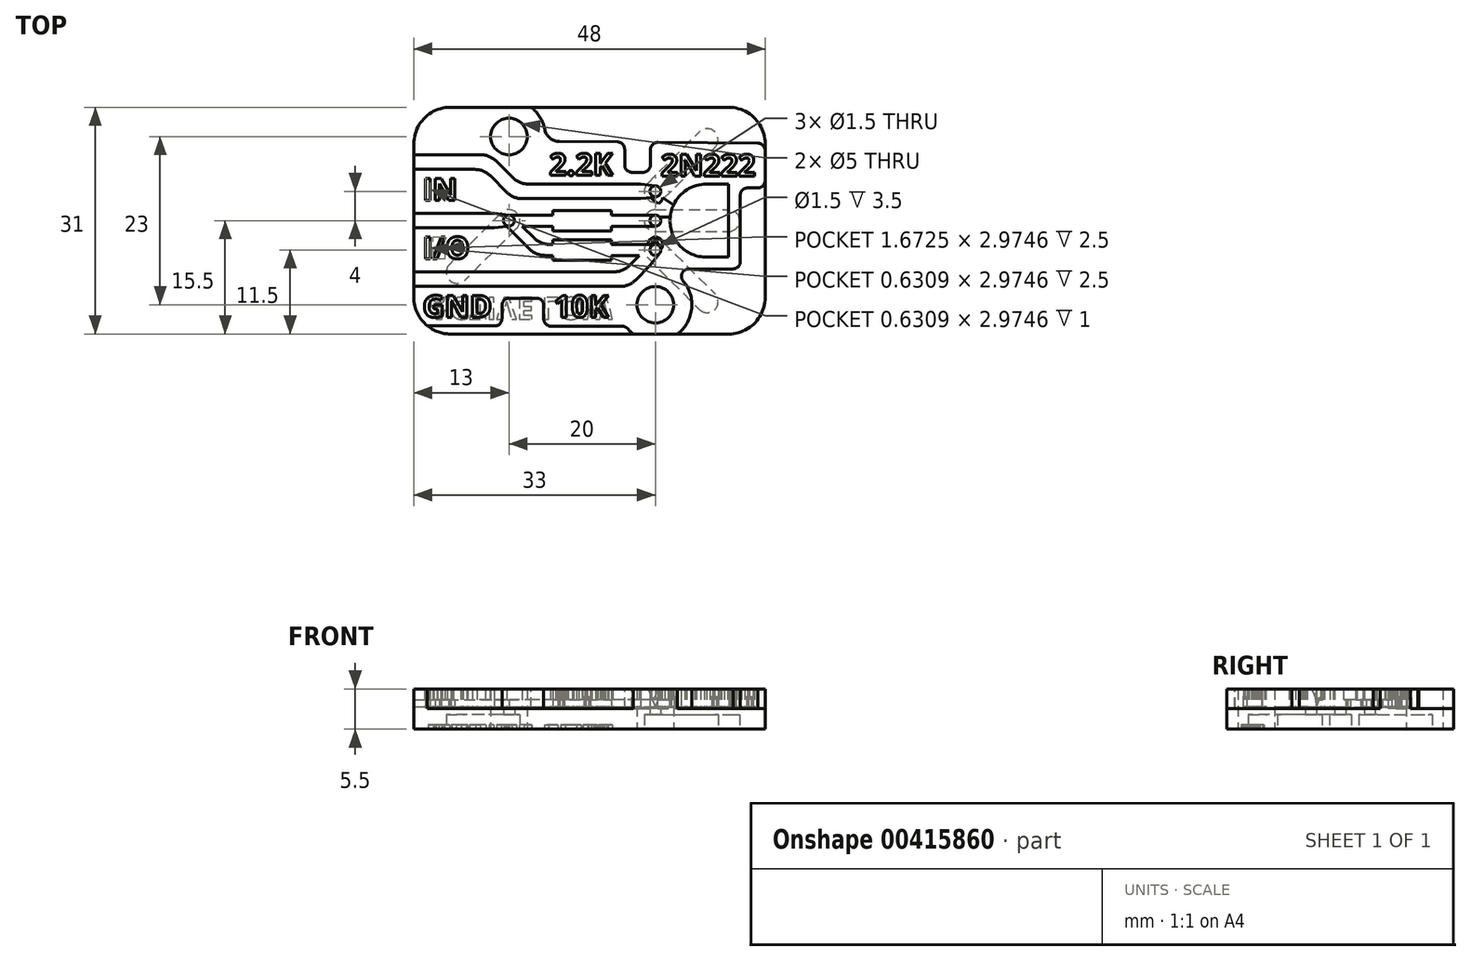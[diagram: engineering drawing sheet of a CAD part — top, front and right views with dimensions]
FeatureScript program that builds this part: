
annotation { "Feature Type Name" : "Feature", "Feature Type Description" : "" }
export const myFeature = defineFeature(function(context is Context, id is Id, definition is map)
    precondition{}
    {
        {
            var Q0;
            Q0=qCreatedBy(makeId("Top.planeOp"),FACE);
            var sketch = newSketch(context, id + "F0", { "sketchPlane" : qUnion([Q0])});
            skLineSegment(sketch, "E0.bottom", {"start": v(-11.3, 15.5) * mm, "end": v(36.7, 15.5) * mm});
            skLineSegment(sketch, "E0.top", {"start": v(-11.3, -15.5) * mm, "end": v(36.7, -15.5) * mm});
            skLineSegment(sketch, "E0.left", {"start": v(-11.3, 15.5) * mm, "end": v(-11.3, -15.5) * mm});
            skLineSegment(sketch, "E0.right", {"start": v(36.7, 15.5) * mm, "end": v(36.7, -15.5) * mm});
            skCircle(sketch, "E1", {"center": v(21.7, 4) * mm, "radius": 0.75 * mm});
            skCircle(sketch, "E2", {"center": v(21.7, 0) * mm, "radius": 0.75 * mm});
            skCircle(sketch, "E3", {"center": v(21.7, -4) * mm, "radius": 0.75 * mm});
            skLineSegment(sketch, "E4", {"start": v(31.7, 5) * mm, "end": v(31.7, -5) * mm});
            skLineSegment(sketch, "E5.bottom", {"start": v(31.7, 5) * mm, "end": v(28.7, 5) * mm});
            skLineSegment(sketch, "E5.top", {"start": v(31.7, -5) * mm, "end": v(28.7, -5) * mm});
            skLineSegment(sketch, "E5.right", {"start": v(28.7, 5) * mm, "end": v(28.7, -5) * mm});
            skCircle(sketch, "E6", {"center": v(1.7, 0) * mm, "radius": 0.75 * mm});
            skPoint(sketch, "E7", {"position": v(4.07, -2) * mm});
            skPoint(sketch, "E8", {"position": v(-1.03, 0) * mm});
            skLineSegment(sketch, "E9", {"start": v(21.7, 0) * mm, "end": v(1.7, 0) * mm});
            skPoint(sketch, "E10", {"position": v(13.7, 0) * mm});
            skLineSegment(sketch, "E11", {"start": v(7.7, 0) * mm, "end": v(7.7, 1.4) * mm});
            skLineSegment(sketch, "E12", {"start": v(7.7, 1.4) * mm, "end": v(15.7, 1.4) * mm});
            skLineSegment(sketch, "E13", {"start": v(15.7, 1.4) * mm, "end": v(15.7, -1.4) * mm});
            skLineSegment(sketch, "E14", {"start": v(15.7, -1.4) * mm, "end": v(7.7, -1.4) * mm});
            skLineSegment(sketch, "E15", {"start": v(7.7, -1.4) * mm, "end": v(7.7, 0) * mm});
            skLineSegment(sketch, "E16", {"start": v(1.7, 0) * mm, "end": v(5.7, -4) * mm});
            skLineSegment(sketch, "E17", {"start": v(5.7, -4) * mm, "end": v(21.7, -4) * mm});
            skLineSegment(sketch, "E18", {"start": v(1.7, 0) * mm, "end": v(1.7, 0.75) * mm});
            skLineSegment(sketch, "E19", {"start": v(21.7, 0.75) * mm, "end": v(1.7, 0.75) * mm});
            skLineSegment(sketch, "E20", {"start": v(1.7, 0) * mm, "end": v(1.7, -0.75) * mm});
            skLineSegment(sketch, "E21", {"start": v(1.7, -0.75) * mm, "end": v(21.7, -0.75) * mm});
            skLineSegment(sketch, "E22.bottom", {"start": v(7.7, -2.6) * mm, "end": v(15.7, -2.6) * mm});
            skLineSegment(sketch, "E22.top", {"start": v(7.7, -5.4) * mm, "end": v(15.7, -5.4) * mm});
            skLineSegment(sketch, "E22.left", {"start": v(7.7, -2.6) * mm, "end": v(7.7, -5.4) * mm});
            skLineSegment(sketch, "E22.right", {"start": v(15.7, -2.6) * mm, "end": v(15.7, -5.4) * mm});
            skLineSegment(sketch, "E23", {"start": v(21.7, -4) * mm, "end": v(21.7, -3.25) * mm});
            skLineSegment(sketch, "E24", {"start": v(21.7, -3.25) * mm, "end": v(21.7, -4.75) * mm});
            skLineSegment(sketch, "E25", {"start": v(21.7, -4.75) * mm, "end": v(5.38, -4.75) * mm});
            skLineSegment(sketch, "E26", {"start": v(21.7, -3.25) * mm, "end": v(6, -3.25) * mm});
            skLineSegment(sketch, "E27", {"start": v(6, -3.25) * mm, "end": v(2.22, 0.53) * mm});
            skLineSegment(sketch, "E28", {"start": v(5.38, -4.75) * mm, "end": v(1.16, -0.53) * mm});
            skPoint(sketch, "E29", {"position": v(11.7, 0) * mm});
            skPoint(sketch, "E30", {"position": v(11.7, 1.4) * mm});
            skPoint(sketch, "E31", {"position": v(11.7, -2.6) * mm});
            skLineSegment(sketch, "E32.bottom", {"start": v(19.7, 5) * mm, "end": v(0.28, 5) * mm});
            skLineSegment(sketch, "E32.top", {"start": v(19.7, 3) * mm, "end": v(2.28, 3) * mm});
            skLineSegment(sketch, "E32.left", {"start": v(19.7, 5) * mm, "end": v(19.7, 3) * mm});
            skLineSegment(sketch, "E32.right", {"start": v(-11.3, 5) * mm, "end": v(-11.3, 3) * mm});
            skLineSegment(sketch, "E33.bottom", {"start": v(-11.3, -7) * mm, "end": v(17.7, -7) * mm});
            skLineSegment(sketch, "E33.top", {"start": v(-11.3, -9) * mm, "end": v(17.7, -9) * mm});
            skLineSegment(sketch, "E33.left", {"start": v(-11.3, -7) * mm, "end": v(-11.3, -9) * mm});
            skLineSegment(sketch, "E33.right", {"start": v(17.7, -7) * mm, "end": v(17.7, -9) * mm});
            skLineSegment(sketch, "E34.bottom", {"start": v(-11.3, 1) * mm, "end": v(-0.3, 1) * mm});
            skLineSegment(sketch, "E34.top", {"start": v(-11.3, -1) * mm, "end": v(-0.3, -1) * mm});
            skLineSegment(sketch, "E34.left", {"start": v(-11.3, 1) * mm, "end": v(-11.3, -1) * mm});
            skLineSegment(sketch, "E34.right", {"start": v(-0.3, 1) * mm, "end": v(-0.3, -1) * mm});
            skPoint(sketch, "E35", {"position": v(19.7, 4) * mm});
            skLineSegment(sketch, "E36", {"start": v(19.7, 5) * mm, "end": v(21.78, 4.74) * mm});
            skLineSegment(sketch, "E37", {"start": v(21.78, 4.74) * mm, "end": v(21.78, 3.26) * mm});
            skLineSegment(sketch, "E38", {"start": v(21.78, 3.26) * mm, "end": v(19.7, 3) * mm});
            skPoint(sketch, "E39", {"position": v(-0.3, 0) * mm});
            skLineSegment(sketch, "E40", {"start": v(-0.3, 1) * mm, "end": v(1.78, 0.74) * mm});
            skLineSegment(sketch, "E41", {"start": v(1.78, 0.74) * mm, "end": v(1.78, -0.74) * mm});
            skLineSegment(sketch, "E42", {"start": v(1.78, -0.74) * mm, "end": v(-0.3, -1) * mm});
            skLineSegment(sketch, "E43", {"start": v(21.7, -4) * mm, "end": v(17.7, -8) * mm});
            skLineSegment(sketch, "E44", {"start": v(19.57, -4.7) * mm, "end": v(20.99, -6.12) * mm});
            skLineSegment(sketch, "E45", {"start": v(19.57, -4.7) * mm, "end": v(17.28, -7) * mm});
            skLineSegment(sketch, "E46", {"start": v(20.99, -6.12) * mm, "end": v(18.1, -9) * mm});
            skLineSegment(sketch, "E47", {"start": v(17.7, -9) * mm, "end": v(18.1, -9) * mm});
            skLineSegment(sketch, "E48", {"start": v(19.57, -4.7) * mm, "end": v(21.23, -3.4) * mm});
            skLineSegment(sketch, "E49", {"start": v(21.23, -3.4) * mm, "end": v(22.28, -4.46) * mm});
            skLineSegment(sketch, "E50", {"start": v(22.28, -4.46) * mm, "end": v(20.99, -6.12) * mm});
            skText(sketch, "E51", { "text": "I/O", "fontName": "OpenSans-Bold.ttf"});
            skLineSegment(sketch, "E52", {"start": v(19.7, 4) * mm, "end": v(1.28, 4) * mm});
            skLineSegment(sketch, "E53", {"start": v(1.28, 4) * mm, "end": v(2.7, 4) * mm});
            skLineSegment(sketch, "E54", {"start": v(2.7, 4) * mm, "end": v(-1.3, 8) * mm});
            skLineSegment(sketch, "E55", {"start": v(-1.3, 8) * mm, "end": v(-11.3, 8) * mm});
            skLineSegment(sketch, "E56.bottom", {"start": v(-11.3, 9) * mm, "end": v(-0.9, 9) * mm});
            skLineSegment(sketch, "E56.top", {"start": v(-11.3, 7) * mm, "end": v(-1.72, 7) * mm});
            skLineSegment(sketch, "E56.left", {"start": v(-11.3, 9) * mm, "end": v(-11.3, 7) * mm});
            skLineSegment(sketch, "E57", {"start": v(3.1, 5) * mm, "end": v(-0.9, 9) * mm});
            skLineSegment(sketch, "E58", {"start": v(2.28, 3) * mm, "end": v(-1.72, 7) * mm});
            skPoint(sketch, "E58.endSnap0", {"position": v(-2.42, 6.98) * mm});
            skPoint(sketch, "E59.orphan", {"position": v(-2.42, 7.7) * mm});
            skPoint(sketch, "E60.orphan", {"position": v(-11.3, 4) * mm});
            skText(sketch, "E61", { "text": "IN", "fontName": "OpenSans-Bold.ttf"});
            skText(sketch, "E62", { "text": "GND", "fontName": "OpenSans-Bold.ttf"});
            skText(sketch, "E63", { "text": "2N222", "fontName": "OpenSans-Bold.ttf"});
            skArc(sketch, "E64", {"start": v(28.7, 5) * mm, "mid": v(23.7, 0) * mm, "end": v(28.7, -5) * mm});
            skText(sketch, "E65", { "text": "10K", "fontName": "OpenSans-Bold.ttf"});
            skText(sketch, "E66", { "text": "2.2K", "fontName": "OpenSans-Bold.ttf"});
            skPoint(sketch, "E67", {"position": v(36.7, 0) * mm});
            const initialGuessF0  = {"E51": [-0.0101, -0.0052, 1, 0, 0.003], "E61": [-0.0101, 0.0028, 1, 0, 0.003], "E62": [-0.0101, -0.0132, 1, 0, 0.003], "E63": [0.02246, 0.00607, 1, 0, 0.003], "E65": [0.0078, -0.0132, 1, 0, 0.003], "E66": [0.0072, 0.0062, 1, 0, 0.003]};
            skSetInitialGuess(sketch, initialGuessF0);
            skSolve(sketch);
        }
        {
            var Q0;
            {var subQ22=sQuery(id+"F0.wireOp",EDGE,"E0.bottom");Q0=makeQuery(id+"F0.imprint","IMPRINT",FACE,{"disambiguationData":[TD([[makeQuery(id+"F0.imprint","IMPRINT",EDGE,{"derivedFrom":subQ22}),-1.0]])]});}
            var Q1;
            {var subQ14=sQuery(id+"F0.wireOp",EDGE,"E22.top");Q1=makeQuery(id+"F0.imprint","IMPRINT",FACE,{"disambiguationData":[TD([[makeQuery(id+"F0.imprint","IMPRINT",EDGE,{"derivedFrom":subQ14}),-1.0]])]});}
            var Q2;
            Q2=makeQuery(id+"F0.imprint","IMPRINT",FACE,{"disambiguationData":[TD([[makeQuery(id+"F0.imprint","IMPRINT",EDGE,{"derivedFrom":sQuery(id+"F0.wireOp",EDGE,"E51.sketch_text.stroke-16")}),1.0]])]});
            var Q3;
            Q3=makeQuery(id+"F0.imprint","IMPRINT",FACE,{"disambiguationData":[TD([[makeQuery(id+"F0.imprint","IMPRINT",EDGE,{"derivedFrom":sQuery(id+"F0.wireOp",EDGE,"E62.sketch_text.stroke-40")}),1.0]])]});
            var Q4;
            Q4=makeQuery(id+"F0.imprint","IMPRINT",FACE,{"disambiguationData":[TD([[makeQuery(id+"F0.imprint","IMPRINT",EDGE,{"derivedFrom":sQuery(id+"F0.wireOp",EDGE,"E65.sketch_text.stroke-18")}),1.0]])]});
            extrude(context, id + "F1", {"entities" : qUnion([Q0, Q1, Q2, Q3, Q4]), "depth" : (2.5 + 3) * mm});
        }
        {
            var Q0;
            Q0=makeQuery(id+"F1.opExtrude","CAP_FACE",FACE,{"disambiguationData":[OSD([sQuery(id+"F0.wireOp",EDGE,"E0.bottom"),sQuery(id+"F0.wireOp",EDGE,"E0.top"),sQuery(id+"F0.wireOp",EDGE,"E0.left"),sQuery(id+"F0.wireOp",EDGE,"E0.right"),sQuery(id+"F0.wireOp",EDGE,"E1"),sQuery(id+"F0.wireOp",EDGE,"E2"),sQuery(id+"F0.wireOp",EDGE,"E3"),sQuery(id+"F0.wireOp",EDGE,"E5.bottom"),sQuery(id+"F0.wireOp",EDGE,"E5.top"),sQuery(id+"F0.wireOp",EDGE,"E4"),sQuery(id+"F0.wireOp",EDGE,"E11"),sQuery(id+"F0.wireOp",EDGE,"E12"),sQuery(id+"F0.wireOp",EDGE,"E13"),sQuery(id+"F0.wireOp",EDGE,"E14"),sQuery(id+"F0.wireOp",EDGE,"E15"),sQuery(id+"F0.wireOp",EDGE,"E19"),sQuery(id+"F0.wireOp",EDGE,"E21"),sQuery(id+"F0.wireOp",EDGE,"E22.bottom"),sQuery(id+"F0.wireOp",EDGE,"E22.left"),sQuery(id+"F0.wireOp",EDGE,"E22.right"),sQuery(id+"F0.wireOp",EDGE,"E26"),sQuery(id+"F0.wireOp",EDGE,"E27"),sQuery(id+"F0.wireOp",EDGE,"E32.bottom"),sQuery(id+"F0.wireOp",EDGE,"E32.top"),sQuery(id+"F0.wireOp",EDGE,"E32.right"),sQuery(id+"F0.wireOp",EDGE,"E33.top"),sQuery(id+"F0.wireOp",EDGE,"E34.bottom"),sQuery(id+"F0.wireOp",EDGE,"E36"),sQuery(id+"F0.wireOp",EDGE,"E38"),sQuery(id+"F0.wireOp",EDGE,"E40"),sQuery(id+"F0.wireOp",EDGE,"E46"),sQuery(id+"F0.wireOp",EDGE,"E47"),sQuery(id+"F0.wireOp",EDGE,"E50"),sQuery(id+"F0.wireOp",EDGE,"E56.bottom"),sQuery(id+"F0.wireOp",EDGE,"E56.top"),sQuery(id+"F0.wireOp",EDGE,"E57"),sQuery(id+"F0.wireOp",EDGE,"E58"),sQuery(id+"F0.wireOp",EDGE,"E61.sketch_text.stroke-0"),sQuery(id+"F0.wireOp",EDGE,"E61.sketch_text.stroke-1"),sQuery(id+"F0.wireOp",EDGE,"E61.sketch_text.stroke-2"),sQuery(id+"F0.wireOp",EDGE,"E61.sketch_text.stroke-3"),sQuery(id+"F0.wireOp",EDGE,"E61.sketch_text.stroke-4"),sQuery(id+"F0.wireOp",EDGE,"E61.sketch_text.stroke-5"),sQuery(id+"F0.wireOp",EDGE,"E61.sketch_text.stroke-6"),sQuery(id+"F0.wireOp",EDGE,"E61.sketch_text.stroke-7"),sQuery(id+"F0.wireOp",EDGE,"E61.sketch_text.stroke-8"),sQuery(id+"F0.wireOp",EDGE,"E61.sketch_text.stroke-9"),sQuery(id+"F0.wireOp",EDGE,"E61.sketch_text.stroke-10"),sQuery(id+"F0.wireOp",EDGE,"E61.sketch_text.stroke-11"),sQuery(id+"F0.wireOp",EDGE,"E61.sketch_text.stroke-12"),sQuery(id+"F0.wireOp",EDGE,"E61.sketch_text.stroke-13"),sQuery(id+"F0.wireOp",EDGE,"E61.sketch_text.stroke-14"),sQuery(id+"F0.wireOp",EDGE,"E61.sketch_text.stroke-15"),sQuery(id+"F0.wireOp",EDGE,"E61.sketch_text.stroke-16"),sQuery(id+"F0.wireOp",EDGE,"E61.sketch_text.stroke-17"),sQuery(id+"F0.wireOp",EDGE,"E62.sketch_text.stroke-0"),sQuery(id+"F0.wireOp",EDGE,"E62.sketch_text.stroke-1"),sQuery(id+"F0.wireOp",EDGE,"E62.sketch_text.stroke-2"),sQuery(id+"F0.wireOp",EDGE,"E62.sketch_text.stroke-3"),sQuery(id+"F0.wireOp",EDGE,"E62.sketch_text.stroke-4"),sQuery(id+"F0.wireOp",EDGE,"E62.sketch_text.stroke-5"),sQuery(id+"F0.wireOp",EDGE,"E62.sketch_text.stroke-6"),sQuery(id+"F0.wireOp",EDGE,"E62.sketch_text.stroke-7"),sQuery(id+"F0.wireOp",EDGE,"E62.sketch_text.stroke-8"),sQuery(id+"F0.wireOp",EDGE,"E62.sketch_text.stroke-9"),sQuery(id+"F0.wireOp",EDGE,"E62.sketch_text.stroke-10"),sQuery(id+"F0.wireOp",EDGE,"E62.sketch_text.stroke-11"),sQuery(id+"F0.wireOp",EDGE,"E62.sketch_text.stroke-12"),sQuery(id+"F0.wireOp",EDGE,"E62.sketch_text.stroke-13"),sQuery(id+"F0.wireOp",EDGE,"E62.sketch_text.stroke-14"),sQuery(id+"F0.wireOp",EDGE,"E62.sketch_text.stroke-15"),sQuery(id+"F0.wireOp",EDGE,"E62.sketch_text.stroke-16"),sQuery(id+"F0.wireOp",EDGE,"E62.sketch_text.stroke-17"),sQuery(id+"F0.wireOp",EDGE,"E62.sketch_text.stroke-18"),sQuery(id+"F0.wireOp",EDGE,"E62.sketch_text.stroke-19"),sQuery(id+"F0.wireOp",EDGE,"E62.sketch_text.stroke-20"),sQuery(id+"F0.wireOp",EDGE,"E62.sketch_text.stroke-21"),sQuery(id+"F0.wireOp",EDGE,"E62.sketch_text.stroke-22"),sQuery(id+"F0.wireOp",EDGE,"E62.sketch_text.stroke-23"),sQuery(id+"F0.wireOp",EDGE,"E62.sketch_text.stroke-24"),sQuery(id+"F0.wireOp",EDGE,"E62.sketch_text.stroke-25"),sQuery(id+"F0.wireOp",EDGE,"E62.sketch_text.stroke-26"),sQuery(id+"F0.wireOp",EDGE,"E62.sketch_text.stroke-27"),sQuery(id+"F0.wireOp",EDGE,"E62.sketch_text.stroke-28"),sQuery(id+"F0.wireOp",EDGE,"E62.sketch_text.stroke-29"),sQuery(id+"F0.wireOp",EDGE,"E62.sketch_text.stroke-30"),sQuery(id+"F0.wireOp",EDGE,"E62.sketch_text.stroke-31"),sQuery(id+"F0.wireOp",EDGE,"E62.sketch_text.stroke-32"),sQuery(id+"F0.wireOp",EDGE,"E62.sketch_text.stroke-33"),sQuery(id+"F0.wireOp",EDGE,"E62.sketch_text.stroke-34"),sQuery(id+"F0.wireOp",EDGE,"E62.sketch_text.stroke-35"),sQuery(id+"F0.wireOp",EDGE,"E62.sketch_text.stroke-36"),sQuery(id+"F0.wireOp",EDGE,"E62.sketch_text.stroke-37"),sQuery(id+"F0.wireOp",EDGE,"E62.sketch_text.stroke-38"),sQuery(id+"F0.wireOp",EDGE,"E62.sketch_text.stroke-39"),sQuery(id+"F0.wireOp",EDGE,"E63.sketch_text.stroke-0"),sQuery(id+"F0.wireOp",EDGE,"E63.sketch_text.stroke-1"),sQuery(id+"F0.wireOp",EDGE,"E63.sketch_text.stroke-2"),sQuery(id+"F0.wireOp",EDGE,"E63.sketch_text.stroke-3"),sQuery(id+"F0.wireOp",EDGE,"E63.sketch_text.stroke-4"),sQuery(id+"F0.wireOp",EDGE,"E63.sketch_text.stroke-5"),sQuery(id+"F0.wireOp",EDGE,"E63.sketch_text.stroke-6"),sQuery(id+"F0.wireOp",EDGE,"E63.sketch_text.stroke-7"),sQuery(id+"F0.wireOp",EDGE,"E63.sketch_text.stroke-8"),sQuery(id+"F0.wireOp",EDGE,"E63.sketch_text.stroke-9"),sQuery(id+"F0.wireOp",EDGE,"E63.sketch_text.stroke-10"),sQuery(id+"F0.wireOp",EDGE,"E63.sketch_text.stroke-11"),sQuery(id+"F0.wireOp",EDGE,"E63.sketch_text.stroke-12"),sQuery(id+"F0.wireOp",EDGE,"E63.sketch_text.stroke-13"),sQuery(id+"F0.wireOp",EDGE,"E63.sketch_text.stroke-14"),sQuery(id+"F0.wireOp",EDGE,"E63.sketch_text.stroke-15"),sQuery(id+"F0.wireOp",EDGE,"E63.sketch_text.stroke-16"),sQuery(id+"F0.wireOp",EDGE,"E63.sketch_text.stroke-17"),sQuery(id+"F0.wireOp",EDGE,"E63.sketch_text.stroke-18"),sQuery(id+"F0.wireOp",EDGE,"E63.sketch_text.stroke-19"),sQuery(id+"F0.wireOp",EDGE,"E63.sketch_text.stroke-20"),sQuery(id+"F0.wireOp",EDGE,"E63.sketch_text.stroke-21"),sQuery(id+"F0.wireOp",EDGE,"E63.sketch_text.stroke-22"),sQuery(id+"F0.wireOp",EDGE,"E63.sketch_text.stroke-23"),sQuery(id+"F0.wireOp",EDGE,"E63.sketch_text.stroke-24"),sQuery(id+"F0.wireOp",EDGE,"E63.sketch_text.stroke-25"),sQuery(id+"F0.wireOp",EDGE,"E63.sketch_text.stroke-26"),sQuery(id+"F0.wireOp",EDGE,"E63.sketch_text.stroke-27"),sQuery(id+"F0.wireOp",EDGE,"E63.sketch_text.stroke-28"),sQuery(id+"F0.wireOp",EDGE,"E63.sketch_text.stroke-29"),sQuery(id+"F0.wireOp",EDGE,"E63.sketch_text.stroke-30"),sQuery(id+"F0.wireOp",EDGE,"E63.sketch_text.stroke-31"),sQuery(id+"F0.wireOp",EDGE,"E63.sketch_text.stroke-32"),sQuery(id+"F0.wireOp",EDGE,"E63.sketch_text.stroke-33"),sQuery(id+"F0.wireOp",EDGE,"E63.sketch_text.stroke-34"),sQuery(id+"F0.wireOp",EDGE,"E63.sketch_text.stroke-35"),sQuery(id+"F0.wireOp",EDGE,"E63.sketch_text.stroke-36"),sQuery(id+"F0.wireOp",EDGE,"E63.sketch_text.stroke-37"),sQuery(id+"F0.wireOp",EDGE,"E63.sketch_text.stroke-38"),sQuery(id+"F0.wireOp",EDGE,"E63.sketch_text.stroke-39"),sQuery(id+"F0.wireOp",EDGE,"E63.sketch_text.stroke-40"),sQuery(id+"F0.wireOp",EDGE,"E63.sketch_text.stroke-41"),sQuery(id+"F0.wireOp",EDGE,"E63.sketch_text.stroke-42"),sQuery(id+"F0.wireOp",EDGE,"E63.sketch_text.stroke-43"),sQuery(id+"F0.wireOp",EDGE,"E63.sketch_text.stroke-44"),sQuery(id+"F0.wireOp",EDGE,"E63.sketch_text.stroke-45"),sQuery(id+"F0.wireOp",EDGE,"E63.sketch_text.stroke-46"),sQuery(id+"F0.wireOp",EDGE,"E63.sketch_text.stroke-47"),sQuery(id+"F0.wireOp",EDGE,"E63.sketch_text.stroke-48"),sQuery(id+"F0.wireOp",EDGE,"E63.sketch_text.stroke-49"),sQuery(id+"F0.wireOp",EDGE,"E63.sketch_text.stroke-50"),sQuery(id+"F0.wireOp",EDGE,"E63.sketch_text.stroke-51"),sQuery(id+"F0.wireOp",EDGE,"E63.sketch_text.stroke-52"),sQuery(id+"F0.wireOp",EDGE,"E63.sketch_text.stroke-53"),sQuery(id+"F0.wireOp",EDGE,"E63.sketch_text.stroke-54"),sQuery(id+"F0.wireOp",EDGE,"E63.sketch_text.stroke-55"),sQuery(id+"F0.wireOp",EDGE,"E63.sketch_text.stroke-56"),sQuery(id+"F0.wireOp",EDGE,"E63.sketch_text.stroke-57"),sQuery(id+"F0.wireOp",EDGE,"E63.sketch_text.stroke-58"),sQuery(id+"F0.wireOp",EDGE,"E63.sketch_text.stroke-59"),sQuery(id+"F0.wireOp",EDGE,"E63.sketch_text.stroke-60"),sQuery(id+"F0.wireOp",EDGE,"E63.sketch_text.stroke-61"),sQuery(id+"F0.wireOp",EDGE,"E63.sketch_text.stroke-62"),sQuery(id+"F0.wireOp",EDGE,"E63.sketch_text.stroke-63"),sQuery(id+"F0.wireOp",EDGE,"E63.sketch_text.stroke-64"),sQuery(id+"F0.wireOp",EDGE,"E63.sketch_text.stroke-65"),sQuery(id+"F0.wireOp",EDGE,"E63.sketch_text.stroke-66"),sQuery(id+"F0.wireOp",EDGE,"E63.sketch_text.stroke-67"),sQuery(id+"F0.wireOp",EDGE,"E63.sketch_text.stroke-68"),sQuery(id+"F0.wireOp",EDGE,"E63.sketch_text.stroke-69"),sQuery(id+"F0.wireOp",EDGE,"E63.sketch_text.stroke-70"),sQuery(id+"F0.wireOp",EDGE,"E63.sketch_text.stroke-71"),sQuery(id+"F0.wireOp",EDGE,"E63.sketch_text.stroke-72"),sQuery(id+"F0.wireOp",EDGE,"E63.sketch_text.stroke-73"),sQuery(id+"F0.wireOp",EDGE,"E63.sketch_text.stroke-74"),sQuery(id+"F0.wireOp",EDGE,"E63.sketch_text.stroke-75"),sQuery(id+"F0.wireOp",EDGE,"E63.sketch_text.stroke-76"),sQuery(id+"F0.wireOp",EDGE,"E63.sketch_text.stroke-77"),sQuery(id+"F0.wireOp",EDGE,"E63.sketch_text.stroke-78"),sQuery(id+"F0.wireOp",EDGE,"E63.sketch_text.stroke-79"),sQuery(id+"F0.wireOp",EDGE,"E63.sketch_text.stroke-80"),sQuery(id+"F0.wireOp",EDGE,"E63.sketch_text.stroke-81"),sQuery(id+"F0.wireOp",EDGE,"E63.sketch_text.stroke-82"),sQuery(id+"F0.wireOp",EDGE,"E63.sketch_text.stroke-83"),sQuery(id+"F0.wireOp",EDGE,"E63.sketch_text.stroke-84"),sQuery(id+"F0.wireOp",EDGE,"E63.sketch_text.stroke-85"),sQuery(id+"F0.wireOp",EDGE,"E63.sketch_text.stroke-86"),sQuery(id+"F0.wireOp",EDGE,"E63.sketch_text.stroke-87"),sQuery(id+"F0.wireOp",EDGE,"E63.sketch_text.stroke-88"),sQuery(id+"F0.wireOp",EDGE,"E63.sketch_text.stroke-89"),sQuery(id+"F0.wireOp",EDGE,"E63.sketch_text.stroke-90"),sQuery(id+"F0.wireOp",EDGE,"E63.sketch_text.stroke-91"),sQuery(id+"F0.wireOp",EDGE,"E63.sketch_text.stroke-92"),sQuery(id+"F0.wireOp",EDGE,"E63.sketch_text.stroke-93"),sQuery(id+"F0.wireOp",EDGE,"E63.sketch_text.stroke-94"),sQuery(id+"F0.wireOp",EDGE,"E63.sketch_text.stroke-95"),sQuery(id+"F0.wireOp",EDGE,"E63.sketch_text.stroke-96"),sQuery(id+"F0.wireOp",EDGE,"E63.sketch_text.stroke-97"),sQuery(id+"F0.wireOp",EDGE,"E63.sketch_text.stroke-98"),sQuery(id+"F0.wireOp",EDGE,"E63.sketch_text.stroke-99"),sQuery(id+"F0.wireOp",EDGE,"E63.sketch_text.stroke-100"),sQuery(id+"F0.wireOp",EDGE,"E63.sketch_text.stroke-101"),sQuery(id+"F0.wireOp",EDGE,"E63.sketch_text.stroke-102"),sQuery(id+"F0.wireOp",EDGE,"E63.sketch_text.stroke-103"),sQuery(id+"F0.wireOp",EDGE,"E63.sketch_text.stroke-104"),sQuery(id+"F0.wireOp",EDGE,"E63.sketch_text.stroke-105"),sQuery(id+"F0.wireOp",EDGE,"E63.sketch_text.stroke-106"),sQuery(id+"F0.wireOp",EDGE,"E63.sketch_text.stroke-107"),sQuery(id+"F0.wireOp",EDGE,"E63.sketch_text.stroke-108"),sQuery(id+"F0.wireOp",EDGE,"E63.sketch_text.stroke-109"),sQuery(id+"F0.wireOp",EDGE,"E64"),sQuery(id+"F0.wireOp",EDGE,"E65.sketch_text.stroke-0"),sQuery(id+"F0.wireOp",EDGE,"E65.sketch_text.stroke-1"),sQuery(id+"F0.wireOp",EDGE,"E65.sketch_text.stroke-2"),sQuery(id+"F0.wireOp",EDGE,"E65.sketch_text.stroke-3"),sQuery(id+"F0.wireOp",EDGE,"E65.sketch_text.stroke-4"),sQuery(id+"F0.wireOp",EDGE,"E65.sketch_text.stroke-5"),sQuery(id+"F0.wireOp",EDGE,"E65.sketch_text.stroke-6"),sQuery(id+"F0.wireOp",EDGE,"E65.sketch_text.stroke-7"),sQuery(id+"F0.wireOp",EDGE,"E65.sketch_text.stroke-8"),sQuery(id+"F0.wireOp",EDGE,"E65.sketch_text.stroke-9"),sQuery(id+"F0.wireOp",EDGE,"E65.sketch_text.stroke-10"),sQuery(id+"F0.wireOp",EDGE,"E65.sketch_text.stroke-11"),sQuery(id+"F0.wireOp",EDGE,"E65.sketch_text.stroke-12"),sQuery(id+"F0.wireOp",EDGE,"E65.sketch_text.stroke-13"),sQuery(id+"F0.wireOp",EDGE,"E65.sketch_text.stroke-14"),sQuery(id+"F0.wireOp",EDGE,"E65.sketch_text.stroke-15"),sQuery(id+"F0.wireOp",EDGE,"E65.sketch_text.stroke-16"),sQuery(id+"F0.wireOp",EDGE,"E65.sketch_text.stroke-17"),sQuery(id+"F0.wireOp",EDGE,"E65.sketch_text.stroke-26"),sQuery(id+"F0.wireOp",EDGE,"E65.sketch_text.stroke-27"),sQuery(id+"F0.wireOp",EDGE,"E65.sketch_text.stroke-28"),sQuery(id+"F0.wireOp",EDGE,"E65.sketch_text.stroke-29"),sQuery(id+"F0.wireOp",EDGE,"E65.sketch_text.stroke-30"),sQuery(id+"F0.wireOp",EDGE,"E65.sketch_text.stroke-31"),sQuery(id+"F0.wireOp",EDGE,"E65.sketch_text.stroke-32"),sQuery(id+"F0.wireOp",EDGE,"E65.sketch_text.stroke-33"),sQuery(id+"F0.wireOp",EDGE,"E65.sketch_text.stroke-34"),sQuery(id+"F0.wireOp",EDGE,"E65.sketch_text.stroke-35"),sQuery(id+"F0.wireOp",EDGE,"E65.sketch_text.stroke-36"),sQuery(id+"F0.wireOp",EDGE,"E65.sketch_text.stroke-37"),sQuery(id+"F0.wireOp",EDGE,"E65.sketch_text.stroke-38"),sQuery(id+"F0.wireOp",EDGE,"E66.sketch_text.stroke-0"),sQuery(id+"F0.wireOp",EDGE,"E66.sketch_text.stroke-1"),sQuery(id+"F0.wireOp",EDGE,"E66.sketch_text.stroke-2"),sQuery(id+"F0.wireOp",EDGE,"E66.sketch_text.stroke-3"),sQuery(id+"F0.wireOp",EDGE,"E66.sketch_text.stroke-4"),sQuery(id+"F0.wireOp",EDGE,"E66.sketch_text.stroke-5"),sQuery(id+"F0.wireOp",EDGE,"E66.sketch_text.stroke-6"),sQuery(id+"F0.wireOp",EDGE,"E66.sketch_text.stroke-7"),sQuery(id+"F0.wireOp",EDGE,"E66.sketch_text.stroke-8"),sQuery(id+"F0.wireOp",EDGE,"E66.sketch_text.stroke-9"),sQuery(id+"F0.wireOp",EDGE,"E66.sketch_text.stroke-10"),sQuery(id+"F0.wireOp",EDGE,"E66.sketch_text.stroke-11"),sQuery(id+"F0.wireOp",EDGE,"E66.sketch_text.stroke-12"),sQuery(id+"F0.wireOp",EDGE,"E66.sketch_text.stroke-13"),sQuery(id+"F0.wireOp",EDGE,"E66.sketch_text.stroke-14"),sQuery(id+"F0.wireOp",EDGE,"E66.sketch_text.stroke-15"),sQuery(id+"F0.wireOp",EDGE,"E66.sketch_text.stroke-16"),sQuery(id+"F0.wireOp",EDGE,"E66.sketch_text.stroke-17"),sQuery(id+"F0.wireOp",EDGE,"E66.sketch_text.stroke-18"),sQuery(id+"F0.wireOp",EDGE,"E66.sketch_text.stroke-19"),sQuery(id+"F0.wireOp",EDGE,"E66.sketch_text.stroke-20"),sQuery(id+"F0.wireOp",EDGE,"E66.sketch_text.stroke-21"),sQuery(id+"F0.wireOp",EDGE,"E66.sketch_text.stroke-22"),sQuery(id+"F0.wireOp",EDGE,"E66.sketch_text.stroke-23"),sQuery(id+"F0.wireOp",EDGE,"E66.sketch_text.stroke-24"),sQuery(id+"F0.wireOp",EDGE,"E66.sketch_text.stroke-25"),sQuery(id+"F0.wireOp",EDGE,"E66.sketch_text.stroke-26"),sQuery(id+"F0.wireOp",EDGE,"E66.sketch_text.stroke-27"),sQuery(id+"F0.wireOp",EDGE,"E66.sketch_text.stroke-28"),sQuery(id+"F0.wireOp",EDGE,"E66.sketch_text.stroke-29"),sQuery(id+"F0.wireOp",EDGE,"E66.sketch_text.stroke-30"),sQuery(id+"F0.wireOp",EDGE,"E66.sketch_text.stroke-31"),sQuery(id+"F0.wireOp",EDGE,"E66.sketch_text.stroke-32"),sQuery(id+"F0.wireOp",EDGE,"E66.sketch_text.stroke-33"),sQuery(id+"F0.wireOp",EDGE,"E66.sketch_text.stroke-34"),sQuery(id+"F0.wireOp",EDGE,"E66.sketch_text.stroke-35"),sQuery(id+"F0.wireOp",EDGE,"E66.sketch_text.stroke-36"),sQuery(id+"F0.wireOp",EDGE,"E66.sketch_text.stroke-37"),sQuery(id+"F0.wireOp",EDGE,"E66.sketch_text.stroke-38"),sQuery(id+"F0.wireOp",EDGE,"E66.sketch_text.stroke-39"),sQuery(id+"F0.wireOp",EDGE,"E66.sketch_text.stroke-40"),sQuery(id+"F0.wireOp",EDGE,"E66.sketch_text.stroke-41"),sQuery(id+"F0.wireOp",EDGE,"E66.sketch_text.stroke-42"),sQuery(id+"F0.wireOp",EDGE,"E66.sketch_text.stroke-43"),sQuery(id+"F0.wireOp",EDGE,"E66.sketch_text.stroke-44"),sQuery(id+"F0.wireOp",EDGE,"E66.sketch_text.stroke-45"),sQuery(id+"F0.wireOp",EDGE,"E66.sketch_text.stroke-46"),sQuery(id+"F0.wireOp",EDGE,"E66.sketch_text.stroke-47"),sQuery(id+"F0.wireOp",EDGE,"E66.sketch_text.stroke-48"),sQuery(id+"F0.wireOp",EDGE,"E66.sketch_text.stroke-49"),sQuery(id+"F0.wireOp",EDGE,"E66.sketch_text.stroke-50"),sQuery(id+"F0.wireOp",EDGE,"E66.sketch_text.stroke-51"),sQuery(id+"F0.wireOp",EDGE,"E66.sketch_text.stroke-52"),sQuery(id+"F0.wireOp",EDGE,"E66.sketch_text.stroke-53"),sQuery(id+"F0.wireOp",EDGE,"E66.sketch_text.stroke-54"),sQuery(id+"F0.wireOp",EDGE,"E66.sketch_text.stroke-55"),sQuery(id+"F0.wireOp",EDGE,"E66.sketch_text.stroke-56"),sQuery(id+"F0.wireOp",EDGE,"E66.sketch_text.stroke-57"),sQuery(id+"F0.wireOp",EDGE,"E66.sketch_text.stroke-58"),sQuery(id+"F0.wireOp",EDGE,"E66.sketch_text.stroke-59"),sQuery(id+"F0.wireOp",EDGE,"E66.sketch_text.stroke-60"),sQuery(id+"F0.wireOp",EDGE,"E66.sketch_text.stroke-61"),sQuery(id+"F0.wireOp",EDGE,"E66.sketch_text.stroke-62"),sQuery(id+"F0.wireOp",EDGE,"E66.sketch_text.stroke-63"),sQuery(id+"F0.wireOp",EDGE,"E66.sketch_text.stroke-64"),sQuery(id+"F0.wireOp",EDGE,"E66.sketch_text.stroke-65"),sQuery(id+"F0.wireOp",EDGE,"E66.sketch_text.stroke-66"),sQuery(id+"F0.wireOp",EDGE,"E66.sketch_text.stroke-67"),sQuery(id+"F0.wireOp",EDGE,"E66.sketch_text.stroke-68")])],"isStart":true});
            var sketch = newSketch(context, id + "F2", { "sketchPlane" : qUnion([Q0])});
            skLineSegment(sketch, "E68.0.0", {"start": v(-1.72, -7) * mm, "end": v(2.28, -3) * mm, "construction": true});
            skLineSegment(sketch, "E68.0.1", {"start": v(2.28, -3) * mm, "end": v(19.7, -3) * mm, "construction": true});
            skLineSegment(sketch, "E68.0.2", {"start": v(19.7, -3) * mm, "end": v(21.78, -3.26) * mm, "construction": true});
            skArc(sketch, "E68.0.3", {"start": v(21.78, -3.26) * mm, "mid": v(22.44, -4) * mm, "end": v(21.78, -4.74) * mm, "construction": true});
            skLineSegment(sketch, "E68.0.4", {"start": v(21.78, -4.74) * mm, "end": v(19.7, -5) * mm, "construction": true});
            skLineSegment(sketch, "E68.0.5", {"start": v(19.7, -5) * mm, "end": v(3.1, -5) * mm, "construction": true});
            skLineSegment(sketch, "E68.0.6", {"start": v(3.1, -5) * mm, "end": v(-0.9, -9) * mm, "construction": true});
            skLineSegment(sketch, "E68.0.7", {"start": v(-0.9, -9) * mm, "end": v(-11.3, -9) * mm, "construction": true});
            skLineSegment(sketch, "E68.0.8", {"start": v(-11.3, -9) * mm, "end": v(-11.3, -15.5) * mm, "construction": true});
            skLineSegment(sketch, "E68.0.9", {"start": v(-11.3, -15.5) * mm, "end": v(36.7, -15.5) * mm, "construction": true});
            skLineSegment(sketch, "E68.0.10", {"start": v(36.7, -15.5) * mm, "end": v(36.7, 15.5) * mm, "construction": true});
            skLineSegment(sketch, "E68.0.11", {"start": v(36.7, 15.5) * mm, "end": v(-11.3, 15.5) * mm, "construction": true});
            skLineSegment(sketch, "E68.0.12", {"start": v(-11.3, 15.5) * mm, "end": v(-11.3, 9) * mm, "construction": true});
            skLineSegment(sketch, "E68.0.13", {"start": v(-11.3, 9) * mm, "end": v(18.1, 9) * mm, "construction": true});
            skLineSegment(sketch, "E68.0.14", {"start": v(18.1, 9) * mm, "end": v(20.99, 6.12) * mm, "construction": true});
            skLineSegment(sketch, "E68.0.15", {"start": v(20.99, 6.12) * mm, "end": v(22.28, 4.46) * mm, "construction": true});
            skArc(sketch, "E68.0.16", {"start": v(22.28, 4.46) * mm, "mid": v(22.37, 3.67) * mm, "end": v(21.7, 3.25) * mm, "construction": true});
            skLineSegment(sketch, "E68.0.17", {"start": v(21.7, 3.25) * mm, "end": v(15.7, 3.25) * mm, "construction": true});
            skLineSegment(sketch, "E68.0.18", {"start": v(15.7, 3.25) * mm, "end": v(15.7, 2.6) * mm, "construction": true});
            skLineSegment(sketch, "E68.0.19", {"start": v(15.7, 2.6) * mm, "end": v(7.7, 2.6) * mm, "construction": true});
            skLineSegment(sketch, "E68.0.20", {"start": v(7.7, 2.6) * mm, "end": v(7.7, 3.25) * mm, "construction": true});
            skLineSegment(sketch, "E68.0.21", {"start": v(7.7, 3.25) * mm, "end": v(6, 3.25) * mm, "construction": true});
            skLineSegment(sketch, "E68.0.22", {"start": v(6, 3.25) * mm, "end": v(3.5, 0.75) * mm, "construction": true});
            skLineSegment(sketch, "E68.0.23", {"start": v(3.5, 0.75) * mm, "end": v(7.7, 0.75) * mm, "construction": true});
            skLineSegment(sketch, "E68.0.24", {"start": v(7.7, 0.75) * mm, "end": v(7.7, 1.4) * mm, "construction": true});
            skLineSegment(sketch, "E68.0.25", {"start": v(7.7, 1.4) * mm, "end": v(15.7, 1.4) * mm, "construction": true});
            skLineSegment(sketch, "E68.0.26", {"start": v(15.7, 1.4) * mm, "end": v(15.7, 0.75) * mm, "construction": true});
            skLineSegment(sketch, "E68.0.27", {"start": v(15.7, 0.75) * mm, "end": v(21.7, 0.75) * mm, "construction": true});
            skArc(sketch, "E68.0.28", {"start": v(21.7, 0.75) * mm, "mid": v(22.44, 0) * mm, "end": v(21.7, -0.75) * mm, "construction": true});
            skLineSegment(sketch, "E68.0.29", {"start": v(21.7, -0.75) * mm, "end": v(15.7, -0.75) * mm, "construction": true});
            skLineSegment(sketch, "E68.0.30", {"start": v(15.7, -0.75) * mm, "end": v(15.7, -1.4) * mm, "construction": true});
            skLineSegment(sketch, "E68.0.31", {"start": v(15.7, -1.4) * mm, "end": v(7.7, -1.4) * mm, "construction": true});
            skLineSegment(sketch, "E68.0.32", {"start": v(7.7, -1.4) * mm, "end": v(7.7, -0.75) * mm, "construction": true});
            skLineSegment(sketch, "E68.0.33", {"start": v(7.7, -0.75) * mm, "end": v(1.74, -0.75) * mm, "construction": true});
            skLineSegment(sketch, "E68.0.34", {"start": v(1.74, -0.75) * mm, "end": v(-0.3, -1) * mm, "construction": true});
            skLineSegment(sketch, "E68.0.35", {"start": v(-0.3, -1) * mm, "end": v(-11.3, -1) * mm, "construction": true});
            skLineSegment(sketch, "E68.0.36", {"start": v(-11.3, -1) * mm, "end": v(-11.3, -7) * mm, "construction": true});
            skLineSegment(sketch, "E68.0.37", {"start": v(-11.3, -7) * mm, "end": v(-1.72, -7) * mm, "construction": true});
            skPoint(sketch, "E69.0", {"position": v(-11.3, -15.5) * mm});
            skLineSegment(sketch, "E70.bottom", {"start": v(36.7, -15.5) * mm, "end": v(-11.3, -15.5) * mm});
            skLineSegment(sketch, "E70.top", {"start": v(36.7, 15.5) * mm, "end": v(-11.3, 15.5) * mm});
            skLineSegment(sketch, "E70.left", {"start": v(36.7, -15.5) * mm, "end": v(36.7, 15.5) * mm});
            skLineSegment(sketch, "E70.right", {"start": v(-11.3, -15.5) * mm, "end": v(-11.3, 15.5) * mm});
            skSolve(sketch);
        }
        {
            var Q0;
            Q0 = qSketchRegion(id + "F2", true);
            extrude(context, id + "F3", {"entities" : qUnion([Q0]), "operationType" : NewBodyOperationType.ADD, "oppositeDirection" : true, "depth" : 3 * mm});
        }
        {
            var Q0;
            {var subQ22=sQuery(id+"F0.wireOp",EDGE,"E0.bottom");Q0=makeQuery(id+"F0.imprint","IMPRINT",FACE,{"disambiguationData":[TD([[makeQuery(id+"F0.imprint","IMPRINT",EDGE,{"derivedFrom":subQ22}),-1.0]])]});}
            var sketch = newSketch(context, id + "F4", { "sketchPlane" : qUnion([Q0])});
            skCircle(sketch, "E71.0", {"center": v(21.7, 4) * mm, "radius": 0.75 * mm});
            skCircle(sketch, "E72.0", {"center": v(21.7, 0) * mm, "radius": 0.75 * mm});
            skCircle(sketch, "E73.0", {"center": v(21.7, -4) * mm, "radius": 0.75 * mm});
            skCircle(sketch, "E74.0", {"center": v(1.7, 0) * mm, "radius": 0.75 * mm});
            skSolve(sketch);
        }
        {
            var Q0;
            {var subQ0=sQuery(id+"F4.wireOp",EDGE,"E71.0");var subQ1=makeQuery(id+"F4.imprint","INTERSECT",VERTEX,{"derivedFrom":[makeQuery(id+"F0.imprint","IMPRINT",EDGE,{"derivedFrom":sQuery(id+"F0.wireOp",EDGE,"E36")}),subQ0]});Q0=makeQuery(id+"F4.imprint","IMPRINT",FACE,{"disambiguationData":[TD([[makeQuery(id+"F4.imprint","IMPRINT",EDGE,{"disambiguationData":[TD([[subQ1,-1.0]])],"derivedFrom":subQ0}),1.0]])]});}
            var Q1;
            {var subQ0=sQuery(id+"F0.wireOp",EDGE,"E2");var subQ1=makeQuery(id+"F0.imprint","INTERSECT",VERTEX,{"derivedFrom":[subQ0,sQuery(id+"F0.wireOp",EDGE,"E19")]});Q1=makeQuery(id+"F0.imprint","IMPRINT",FACE,{"disambiguationData":[TD([[makeQuery(id+"F0.imprint","IMPRINT",EDGE,{"disambiguationData":[TD([[subQ1,-1.0]])],"derivedFrom":subQ0}),1.0]])]});}
            var Q2;
            {var subQ0=sQuery(id+"F4.wireOp",EDGE,"E73.0");var subQ3=makeQuery(id+"F4.imprint","INTERSECT",VERTEX,{"derivedFrom":[makeQuery(id+"F0.imprint","IMPRINT",EDGE,{"derivedFrom":sQuery(id+"F0.wireOp",EDGE,"E50")}),subQ0]});Q2=makeQuery(id+"F4.imprint","IMPRINT",FACE,{"disambiguationData":[TD([[makeQuery(id+"F4.imprint","IMPRINT",EDGE,{"disambiguationData":[TD([[subQ3,1.0]])],"derivedFrom":subQ0}),1.0]])]});}
            var Q3;
            {var subQ0=sQuery(id+"F0.wireOp",EDGE,"E6");var subQ1=makeQuery(id+"F0.imprint","INTERSECT",VERTEX,{"derivedFrom":[subQ0,sQuery(id+"F0.wireOp",EDGE,"E27")]});Q3=makeQuery(id+"F0.imprint","IMPRINT",FACE,{"disambiguationData":[TD([[makeQuery(id+"F0.imprint","IMPRINT",EDGE,{"disambiguationData":[TD([[subQ1,1.0]])],"derivedFrom":subQ0}),1.0]])]});}
            var Q4;
            {var subQ0=sQuery(id+"F0.wireOp",EDGE,"E18");Q4=makeQuery(id+"F0.imprint","IMPRINT",FACE,{"disambiguationData":[TD([[makeQuery(id+"F0.imprint","IMPRINT",EDGE,{"derivedFrom":subQ0}),-1.0]])]});}
            var Q5;
            {var subQ0=sQuery(id+"F0.wireOp",EDGE,"E18");Q5=makeQuery(id+"F0.imprint","IMPRINT",FACE,{"disambiguationData":[TD([[makeQuery(id+"F0.imprint","IMPRINT",EDGE,{"derivedFrom":subQ0}),1.0]])]});}
            var Q6;
            {var subQ1=sQuery(id+"F0.wireOp",EDGE,"E6");var subQ3=sQuery(id+"F0.wireOp",EDGE,"E16");var subQ4=makeQuery(id+"F0.imprint","INTERSECT",VERTEX,{"derivedFrom":[subQ1,subQ3]});Q6=makeQuery(id+"F0.imprint","IMPRINT",FACE,{"disambiguationData":[TD([[makeQuery(id+"F0.imprint","IMPRINT",EDGE,{"disambiguationData":[TD([[subQ4,1.0]])],"derivedFrom":subQ3}),-1.0]])]});}
            var Q7;
            {var subQ0=sQuery(id+"F0.wireOp",EDGE,"E9");var subQ1=sQuery(id+"F0.wireOp",EDGE,"E6");var subQ2=makeQuery(id+"F0.imprint","INTERSECT",VERTEX,{"derivedFrom":[subQ1,subQ0]});Q7=makeQuery(id+"F0.imprint","IMPRINT",FACE,{"disambiguationData":[TD([[makeQuery(id+"F0.imprint","IMPRINT",EDGE,{"disambiguationData":[TD([[subQ2,1.0]])],"derivedFrom":subQ1}),1.0]])]});}
            var Q8;
            {var subQ0=sQuery(id+"F0.wireOp",EDGE,"E20");Q8=makeQuery(id+"F0.imprint","IMPRINT",FACE,{"disambiguationData":[TD([[makeQuery(id+"F0.imprint","IMPRINT",EDGE,{"derivedFrom":subQ0}),1.0]])]});}
            var Q9;
            {var subQ1=sQuery(id+"F0.wireOp",EDGE,"E9");var subQ3=sQuery(id+"F0.wireOp",EDGE,"E41");var subQ4=makeQuery(id+"F0.imprint","INTERSECT",VERTEX,{"derivedFrom":[subQ1,subQ3]});Q9=makeQuery(id+"F0.imprint","IMPRINT",FACE,{"disambiguationData":[TD([[makeQuery(id+"F0.imprint","IMPRINT",EDGE,{"disambiguationData":[TD([[subQ4,-1.0]])],"derivedFrom":subQ3}),-1.0]])]});}
            extrude(context, id + "F5", {"entities" : qUnion([Q0, Q1, Q2, Q3, Q4, Q5, Q6, Q7, Q8, Q9]), "operationType" : NewBodyOperationType.REMOVE, "endBound" : BoundingType.THROUGH_ALL, "depth" : 25 * mm});
        }
        {
            var Q0;
            {var subQ22=sQuery(id+"F0.wireOp",EDGE,"E0.bottom");Q0=makeQuery(id+"F0.imprint","IMPRINT",FACE,{"disambiguationData":[TD([[makeQuery(id+"F0.imprint","IMPRINT",EDGE,{"derivedFrom":subQ22}),-1.0]])]});}
            var sketch = newSketch(context, id + "F6", { "sketchPlane" : qUnion([Q0])});
            skCircle(sketch, "E75.0", {"center": v(21.7, 4) * mm, "radius": 0.75 * mm});
            skCircle(sketch, "E76.0", {"center": v(21.7, 0) * mm, "radius": 0.75 * mm});
            skCircle(sketch, "E77.0", {"center": v(21.7, -4) * mm, "radius": 0.75 * mm});
            skCircle(sketch, "E78.0", {"center": v(1.7, 0) * mm, "radius": 0.75 * mm});
            skLineSegment(sketch, "E79", {"start": v(21.7, 4) * mm, "end": v(28.76, 11.07) * mm});
            skLineSegment(sketch, "E80", {"start": v(21.7, -4) * mm, "end": v(28.76, -11.07) * mm});
            skLineSegment(sketch, "E81", {"start": v(21.7, 0) * mm, "end": v(31.7, 0) * mm});
            skArc(sketch, "E82.0.startCap", {"start": v(20.63, -5.06) * mm, "mid": v(20.63, -2.94) * mm, "end": v(22.75, -2.94) * mm});
            skArc(sketch, "E82.0.endCap", {"start": v(29.83, -10.01) * mm, "mid": v(29.83, -12.13) * mm, "end": v(27.7, -12.13) * mm});
            skLineSegment(sketch, "E82.0.left", {"start": v(22.75, -2.94) * mm, "end": v(29.83, -10.01) * mm});
            skLineSegment(sketch, "E82.0.right", {"start": v(20.63, -5.06) * mm, "end": v(27.7, -12.13) * mm});
            skArc(sketch, "E83.0.startCap", {"start": v(21.7, -1.5) * mm, "mid": v(20.2, 0) * mm, "end": v(21.7, 1.5) * mm});
            skArc(sketch, "E83.0.endCap", {"start": v(31.7, 1.5) * mm, "mid": v(33.2, 0) * mm, "end": v(31.7, -1.5) * mm});
            skLineSegment(sketch, "E83.0.left", {"start": v(21.7, 1.5) * mm, "end": v(31.7, 1.5) * mm});
            skLineSegment(sketch, "E83.0.right", {"start": v(21.7, -1.5) * mm, "end": v(31.7, -1.5) * mm});
            skArc(sketch, "E84.0.startCap", {"start": v(22.75, 2.94) * mm, "mid": v(20.63, 2.94) * mm, "end": v(20.63, 5.06) * mm});
            skArc(sketch, "E84.0.endCap", {"start": v(27.7, 12.13) * mm, "mid": v(29.83, 12.13) * mm, "end": v(29.83, 10.01) * mm});
            skLineSegment(sketch, "E84.0.left", {"start": v(20.63, 5.06) * mm, "end": v(27.7, 12.13) * mm});
            skLineSegment(sketch, "E84.0.right", {"start": v(22.75, 2.94) * mm, "end": v(29.83, 10.01) * mm});
            skLineSegment(sketch, "E85", {"start": v(1.7, 0) * mm, "end": v(-5.38, -7.07) * mm});
            skArc(sketch, "E86.0.startCap", {"start": v(0.63, 1.06) * mm, "mid": v(2.75, 1.06) * mm, "end": v(2.75, -1.06) * mm});
            skArc(sketch, "E86.0.endCap", {"start": v(-4.32, -8.13) * mm, "mid": v(-6.44, -8.13) * mm, "end": v(-6.44, -6.01) * mm});
            skLineSegment(sketch, "E86.0.left", {"start": v(2.75, -1.06) * mm, "end": v(-4.32, -8.13) * mm});
            skLineSegment(sketch, "E86.0.right", {"start": v(0.63, 1.06) * mm, "end": v(-6.44, -6.01) * mm});
            skSolve(sketch);
        }
        {
            var Q0;
            Q0 = qSketchRegion(id + "F6", true);
            extrude(context, id + "F7", {"entities" : qUnion([Q0]), "operationType" : NewBodyOperationType.REMOVE, "depth" : 2 * mm});
        }
        {
            var Q0;
            {var subQ0=sQuery(id+"F0.wireOp",EDGE,"E22.right");var subQ1=sQuery(id+"F0.wireOp",EDGE,"E22.left");var subQ2=sQuery(id+"F0.wireOp",EDGE,"E0.left");Q0=makeQuery(id+"F3.boolean.opBoolean","MERGE",FACE,{"derivedFrom":[makeQuery(id+"F1.opExtrude","CAP_FACE",FACE,{"disambiguationData":[OSD([sQuery(id+"F0.wireOp",EDGE,"E0.bottom"),sQuery(id+"F0.wireOp",EDGE,"E0.top"),subQ2,sQuery(id+"F0.wireOp",EDGE,"E0.right"),sQuery(id+"F0.wireOp",EDGE,"E1"),sQuery(id+"F0.wireOp",EDGE,"E2"),sQuery(id+"F0.wireOp",EDGE,"E3"),sQuery(id+"F0.wireOp",EDGE,"E5.bottom"),sQuery(id+"F0.wireOp",EDGE,"E5.top"),sQuery(id+"F0.wireOp",EDGE,"E4"),sQuery(id+"F0.wireOp",EDGE,"E11"),sQuery(id+"F0.wireOp",EDGE,"E12"),sQuery(id+"F0.wireOp",EDGE,"E13"),sQuery(id+"F0.wireOp",EDGE,"E14"),sQuery(id+"F0.wireOp",EDGE,"E15"),sQuery(id+"F0.wireOp",EDGE,"E19"),sQuery(id+"F0.wireOp",EDGE,"E21"),sQuery(id+"F0.wireOp",EDGE,"E22.bottom"),subQ1,subQ0,sQuery(id+"F0.wireOp",EDGE,"E26"),sQuery(id+"F0.wireOp",EDGE,"E27"),sQuery(id+"F0.wireOp",EDGE,"E32.bottom"),sQuery(id+"F0.wireOp",EDGE,"E32.top"),sQuery(id+"F0.wireOp",EDGE,"E32.right"),sQuery(id+"F0.wireOp",EDGE,"E33.top"),sQuery(id+"F0.wireOp",EDGE,"E34.bottom"),sQuery(id+"F0.wireOp",EDGE,"E36"),sQuery(id+"F0.wireOp",EDGE,"E38"),sQuery(id+"F0.wireOp",EDGE,"E40"),sQuery(id+"F0.wireOp",EDGE,"E46"),sQuery(id+"F0.wireOp",EDGE,"E47"),sQuery(id+"F0.wireOp",EDGE,"E50"),sQuery(id+"F0.wireOp",EDGE,"E56.bottom"),sQuery(id+"F0.wireOp",EDGE,"E56.top"),sQuery(id+"F0.wireOp",EDGE,"E57"),sQuery(id+"F0.wireOp",EDGE,"E58"),sQuery(id+"F0.wireOp",EDGE,"E61.sketch_text.stroke-0"),sQuery(id+"F0.wireOp",EDGE,"E61.sketch_text.stroke-1"),sQuery(id+"F0.wireOp",EDGE,"E61.sketch_text.stroke-2"),sQuery(id+"F0.wireOp",EDGE,"E61.sketch_text.stroke-3"),sQuery(id+"F0.wireOp",EDGE,"E61.sketch_text.stroke-4"),sQuery(id+"F0.wireOp",EDGE,"E61.sketch_text.stroke-5"),sQuery(id+"F0.wireOp",EDGE,"E61.sketch_text.stroke-6"),sQuery(id+"F0.wireOp",EDGE,"E61.sketch_text.stroke-7"),sQuery(id+"F0.wireOp",EDGE,"E61.sketch_text.stroke-8"),sQuery(id+"F0.wireOp",EDGE,"E61.sketch_text.stroke-9"),sQuery(id+"F0.wireOp",EDGE,"E61.sketch_text.stroke-10"),sQuery(id+"F0.wireOp",EDGE,"E61.sketch_text.stroke-11"),sQuery(id+"F0.wireOp",EDGE,"E61.sketch_text.stroke-12"),sQuery(id+"F0.wireOp",EDGE,"E61.sketch_text.stroke-13"),sQuery(id+"F0.wireOp",EDGE,"E61.sketch_text.stroke-14"),sQuery(id+"F0.wireOp",EDGE,"E61.sketch_text.stroke-15"),sQuery(id+"F0.wireOp",EDGE,"E61.sketch_text.stroke-16"),sQuery(id+"F0.wireOp",EDGE,"E61.sketch_text.stroke-17"),sQuery(id+"F0.wireOp",EDGE,"E62.sketch_text.stroke-0"),sQuery(id+"F0.wireOp",EDGE,"E62.sketch_text.stroke-1"),sQuery(id+"F0.wireOp",EDGE,"E62.sketch_text.stroke-2"),sQuery(id+"F0.wireOp",EDGE,"E62.sketch_text.stroke-3"),sQuery(id+"F0.wireOp",EDGE,"E62.sketch_text.stroke-4"),sQuery(id+"F0.wireOp",EDGE,"E62.sketch_text.stroke-5"),sQuery(id+"F0.wireOp",EDGE,"E62.sketch_text.stroke-6"),sQuery(id+"F0.wireOp",EDGE,"E62.sketch_text.stroke-7"),sQuery(id+"F0.wireOp",EDGE,"E62.sketch_text.stroke-8"),sQuery(id+"F0.wireOp",EDGE,"E62.sketch_text.stroke-9"),sQuery(id+"F0.wireOp",EDGE,"E62.sketch_text.stroke-10"),sQuery(id+"F0.wireOp",EDGE,"E62.sketch_text.stroke-11"),sQuery(id+"F0.wireOp",EDGE,"E62.sketch_text.stroke-12"),sQuery(id+"F0.wireOp",EDGE,"E62.sketch_text.stroke-13"),sQuery(id+"F0.wireOp",EDGE,"E62.sketch_text.stroke-14"),sQuery(id+"F0.wireOp",EDGE,"E62.sketch_text.stroke-15"),sQuery(id+"F0.wireOp",EDGE,"E62.sketch_text.stroke-16"),sQuery(id+"F0.wireOp",EDGE,"E62.sketch_text.stroke-17"),sQuery(id+"F0.wireOp",EDGE,"E62.sketch_text.stroke-18"),sQuery(id+"F0.wireOp",EDGE,"E62.sketch_text.stroke-19"),sQuery(id+"F0.wireOp",EDGE,"E62.sketch_text.stroke-20"),sQuery(id+"F0.wireOp",EDGE,"E62.sketch_text.stroke-21"),sQuery(id+"F0.wireOp",EDGE,"E62.sketch_text.stroke-22"),sQuery(id+"F0.wireOp",EDGE,"E62.sketch_text.stroke-23"),sQuery(id+"F0.wireOp",EDGE,"E62.sketch_text.stroke-24"),sQuery(id+"F0.wireOp",EDGE,"E62.sketch_text.stroke-25"),sQuery(id+"F0.wireOp",EDGE,"E62.sketch_text.stroke-26"),sQuery(id+"F0.wireOp",EDGE,"E62.sketch_text.stroke-27"),sQuery(id+"F0.wireOp",EDGE,"E62.sketch_text.stroke-28"),sQuery(id+"F0.wireOp",EDGE,"E62.sketch_text.stroke-29"),sQuery(id+"F0.wireOp",EDGE,"E62.sketch_text.stroke-30"),sQuery(id+"F0.wireOp",EDGE,"E62.sketch_text.stroke-31"),sQuery(id+"F0.wireOp",EDGE,"E62.sketch_text.stroke-32"),sQuery(id+"F0.wireOp",EDGE,"E62.sketch_text.stroke-33"),sQuery(id+"F0.wireOp",EDGE,"E62.sketch_text.stroke-34"),sQuery(id+"F0.wireOp",EDGE,"E62.sketch_text.stroke-35"),sQuery(id+"F0.wireOp",EDGE,"E62.sketch_text.stroke-36"),sQuery(id+"F0.wireOp",EDGE,"E62.sketch_text.stroke-37"),sQuery(id+"F0.wireOp",EDGE,"E62.sketch_text.stroke-38"),sQuery(id+"F0.wireOp",EDGE,"E62.sketch_text.stroke-39"),sQuery(id+"F0.wireOp",EDGE,"E63.sketch_text.stroke-0"),sQuery(id+"F0.wireOp",EDGE,"E63.sketch_text.stroke-1"),sQuery(id+"F0.wireOp",EDGE,"E63.sketch_text.stroke-2"),sQuery(id+"F0.wireOp",EDGE,"E63.sketch_text.stroke-3"),sQuery(id+"F0.wireOp",EDGE,"E63.sketch_text.stroke-4"),sQuery(id+"F0.wireOp",EDGE,"E63.sketch_text.stroke-5"),sQuery(id+"F0.wireOp",EDGE,"E63.sketch_text.stroke-6"),sQuery(id+"F0.wireOp",EDGE,"E63.sketch_text.stroke-7"),sQuery(id+"F0.wireOp",EDGE,"E63.sketch_text.stroke-8"),sQuery(id+"F0.wireOp",EDGE,"E63.sketch_text.stroke-9"),sQuery(id+"F0.wireOp",EDGE,"E63.sketch_text.stroke-10"),sQuery(id+"F0.wireOp",EDGE,"E63.sketch_text.stroke-11"),sQuery(id+"F0.wireOp",EDGE,"E63.sketch_text.stroke-12"),sQuery(id+"F0.wireOp",EDGE,"E63.sketch_text.stroke-13"),sQuery(id+"F0.wireOp",EDGE,"E63.sketch_text.stroke-14"),sQuery(id+"F0.wireOp",EDGE,"E63.sketch_text.stroke-15"),sQuery(id+"F0.wireOp",EDGE,"E63.sketch_text.stroke-16"),sQuery(id+"F0.wireOp",EDGE,"E63.sketch_text.stroke-17"),sQuery(id+"F0.wireOp",EDGE,"E63.sketch_text.stroke-18"),sQuery(id+"F0.wireOp",EDGE,"E63.sketch_text.stroke-19"),sQuery(id+"F0.wireOp",EDGE,"E63.sketch_text.stroke-20"),sQuery(id+"F0.wireOp",EDGE,"E63.sketch_text.stroke-21"),sQuery(id+"F0.wireOp",EDGE,"E63.sketch_text.stroke-22"),sQuery(id+"F0.wireOp",EDGE,"E63.sketch_text.stroke-23"),sQuery(id+"F0.wireOp",EDGE,"E63.sketch_text.stroke-24"),sQuery(id+"F0.wireOp",EDGE,"E63.sketch_text.stroke-25"),sQuery(id+"F0.wireOp",EDGE,"E63.sketch_text.stroke-26"),sQuery(id+"F0.wireOp",EDGE,"E63.sketch_text.stroke-27"),sQuery(id+"F0.wireOp",EDGE,"E63.sketch_text.stroke-28"),sQuery(id+"F0.wireOp",EDGE,"E63.sketch_text.stroke-29"),sQuery(id+"F0.wireOp",EDGE,"E63.sketch_text.stroke-30"),sQuery(id+"F0.wireOp",EDGE,"E63.sketch_text.stroke-31"),sQuery(id+"F0.wireOp",EDGE,"E63.sketch_text.stroke-32"),sQuery(id+"F0.wireOp",EDGE,"E63.sketch_text.stroke-33"),sQuery(id+"F0.wireOp",EDGE,"E63.sketch_text.stroke-34"),sQuery(id+"F0.wireOp",EDGE,"E63.sketch_text.stroke-35"),sQuery(id+"F0.wireOp",EDGE,"E63.sketch_text.stroke-36"),sQuery(id+"F0.wireOp",EDGE,"E63.sketch_text.stroke-37"),sQuery(id+"F0.wireOp",EDGE,"E63.sketch_text.stroke-38"),sQuery(id+"F0.wireOp",EDGE,"E63.sketch_text.stroke-39"),sQuery(id+"F0.wireOp",EDGE,"E63.sketch_text.stroke-40"),sQuery(id+"F0.wireOp",EDGE,"E63.sketch_text.stroke-41"),sQuery(id+"F0.wireOp",EDGE,"E63.sketch_text.stroke-42"),sQuery(id+"F0.wireOp",EDGE,"E63.sketch_text.stroke-43"),sQuery(id+"F0.wireOp",EDGE,"E63.sketch_text.stroke-44"),sQuery(id+"F0.wireOp",EDGE,"E63.sketch_text.stroke-45"),sQuery(id+"F0.wireOp",EDGE,"E63.sketch_text.stroke-46"),sQuery(id+"F0.wireOp",EDGE,"E63.sketch_text.stroke-47"),sQuery(id+"F0.wireOp",EDGE,"E63.sketch_text.stroke-48"),sQuery(id+"F0.wireOp",EDGE,"E63.sketch_text.stroke-49"),sQuery(id+"F0.wireOp",EDGE,"E63.sketch_text.stroke-50"),sQuery(id+"F0.wireOp",EDGE,"E63.sketch_text.stroke-51"),sQuery(id+"F0.wireOp",EDGE,"E63.sketch_text.stroke-52"),sQuery(id+"F0.wireOp",EDGE,"E63.sketch_text.stroke-53"),sQuery(id+"F0.wireOp",EDGE,"E63.sketch_text.stroke-54"),sQuery(id+"F0.wireOp",EDGE,"E63.sketch_text.stroke-55"),sQuery(id+"F0.wireOp",EDGE,"E63.sketch_text.stroke-56"),sQuery(id+"F0.wireOp",EDGE,"E63.sketch_text.stroke-57"),sQuery(id+"F0.wireOp",EDGE,"E63.sketch_text.stroke-58"),sQuery(id+"F0.wireOp",EDGE,"E63.sketch_text.stroke-59"),sQuery(id+"F0.wireOp",EDGE,"E63.sketch_text.stroke-60"),sQuery(id+"F0.wireOp",EDGE,"E63.sketch_text.stroke-61"),sQuery(id+"F0.wireOp",EDGE,"E63.sketch_text.stroke-62"),sQuery(id+"F0.wireOp",EDGE,"E63.sketch_text.stroke-63"),sQuery(id+"F0.wireOp",EDGE,"E63.sketch_text.stroke-64"),sQuery(id+"F0.wireOp",EDGE,"E63.sketch_text.stroke-65"),sQuery(id+"F0.wireOp",EDGE,"E63.sketch_text.stroke-66"),sQuery(id+"F0.wireOp",EDGE,"E63.sketch_text.stroke-67"),sQuery(id+"F0.wireOp",EDGE,"E63.sketch_text.stroke-68"),sQuery(id+"F0.wireOp",EDGE,"E63.sketch_text.stroke-69"),sQuery(id+"F0.wireOp",EDGE,"E63.sketch_text.stroke-70"),sQuery(id+"F0.wireOp",EDGE,"E63.sketch_text.stroke-71"),sQuery(id+"F0.wireOp",EDGE,"E63.sketch_text.stroke-72"),sQuery(id+"F0.wireOp",EDGE,"E63.sketch_text.stroke-73"),sQuery(id+"F0.wireOp",EDGE,"E63.sketch_text.stroke-74"),sQuery(id+"F0.wireOp",EDGE,"E63.sketch_text.stroke-75"),sQuery(id+"F0.wireOp",EDGE,"E63.sketch_text.stroke-76"),sQuery(id+"F0.wireOp",EDGE,"E63.sketch_text.stroke-77"),sQuery(id+"F0.wireOp",EDGE,"E63.sketch_text.stroke-78"),sQuery(id+"F0.wireOp",EDGE,"E63.sketch_text.stroke-79"),sQuery(id+"F0.wireOp",EDGE,"E63.sketch_text.stroke-80"),sQuery(id+"F0.wireOp",EDGE,"E63.sketch_text.stroke-81"),sQuery(id+"F0.wireOp",EDGE,"E63.sketch_text.stroke-82"),sQuery(id+"F0.wireOp",EDGE,"E63.sketch_text.stroke-83"),sQuery(id+"F0.wireOp",EDGE,"E63.sketch_text.stroke-84"),sQuery(id+"F0.wireOp",EDGE,"E63.sketch_text.stroke-85"),sQuery(id+"F0.wireOp",EDGE,"E63.sketch_text.stroke-86"),sQuery(id+"F0.wireOp",EDGE,"E63.sketch_text.stroke-87"),sQuery(id+"F0.wireOp",EDGE,"E63.sketch_text.stroke-88"),sQuery(id+"F0.wireOp",EDGE,"E63.sketch_text.stroke-89"),sQuery(id+"F0.wireOp",EDGE,"E63.sketch_text.stroke-90"),sQuery(id+"F0.wireOp",EDGE,"E63.sketch_text.stroke-91"),sQuery(id+"F0.wireOp",EDGE,"E63.sketch_text.stroke-92"),sQuery(id+"F0.wireOp",EDGE,"E63.sketch_text.stroke-93"),sQuery(id+"F0.wireOp",EDGE,"E63.sketch_text.stroke-94"),sQuery(id+"F0.wireOp",EDGE,"E63.sketch_text.stroke-95"),sQuery(id+"F0.wireOp",EDGE,"E63.sketch_text.stroke-96"),sQuery(id+"F0.wireOp",EDGE,"E63.sketch_text.stroke-97"),sQuery(id+"F0.wireOp",EDGE,"E63.sketch_text.stroke-98"),sQuery(id+"F0.wireOp",EDGE,"E63.sketch_text.stroke-99"),sQuery(id+"F0.wireOp",EDGE,"E63.sketch_text.stroke-100"),sQuery(id+"F0.wireOp",EDGE,"E63.sketch_text.stroke-101"),sQuery(id+"F0.wireOp",EDGE,"E63.sketch_text.stroke-102"),sQuery(id+"F0.wireOp",EDGE,"E63.sketch_text.stroke-103"),sQuery(id+"F0.wireOp",EDGE,"E63.sketch_text.stroke-104"),sQuery(id+"F0.wireOp",EDGE,"E63.sketch_text.stroke-105"),sQuery(id+"F0.wireOp",EDGE,"E63.sketch_text.stroke-106"),sQuery(id+"F0.wireOp",EDGE,"E63.sketch_text.stroke-107"),sQuery(id+"F0.wireOp",EDGE,"E63.sketch_text.stroke-108"),sQuery(id+"F0.wireOp",EDGE,"E63.sketch_text.stroke-109"),sQuery(id+"F0.wireOp",EDGE,"E64"),sQuery(id+"F0.wireOp",EDGE,"E65.sketch_text.stroke-0"),sQuery(id+"F0.wireOp",EDGE,"E65.sketch_text.stroke-1"),sQuery(id+"F0.wireOp",EDGE,"E65.sketch_text.stroke-2"),sQuery(id+"F0.wireOp",EDGE,"E65.sketch_text.stroke-3"),sQuery(id+"F0.wireOp",EDGE,"E65.sketch_text.stroke-4"),sQuery(id+"F0.wireOp",EDGE,"E65.sketch_text.stroke-5"),sQuery(id+"F0.wireOp",EDGE,"E65.sketch_text.stroke-6"),sQuery(id+"F0.wireOp",EDGE,"E65.sketch_text.stroke-7"),sQuery(id+"F0.wireOp",EDGE,"E65.sketch_text.stroke-8"),sQuery(id+"F0.wireOp",EDGE,"E65.sketch_text.stroke-9"),sQuery(id+"F0.wireOp",EDGE,"E65.sketch_text.stroke-10"),sQuery(id+"F0.wireOp",EDGE,"E65.sketch_text.stroke-11"),sQuery(id+"F0.wireOp",EDGE,"E65.sketch_text.stroke-12"),sQuery(id+"F0.wireOp",EDGE,"E65.sketch_text.stroke-13"),sQuery(id+"F0.wireOp",EDGE,"E65.sketch_text.stroke-14"),sQuery(id+"F0.wireOp",EDGE,"E65.sketch_text.stroke-15"),sQuery(id+"F0.wireOp",EDGE,"E65.sketch_text.stroke-16"),sQuery(id+"F0.wireOp",EDGE,"E65.sketch_text.stroke-17"),sQuery(id+"F0.wireOp",EDGE,"E65.sketch_text.stroke-26"),sQuery(id+"F0.wireOp",EDGE,"E65.sketch_text.stroke-27"),sQuery(id+"F0.wireOp",EDGE,"E65.sketch_text.stroke-28"),sQuery(id+"F0.wireOp",EDGE,"E65.sketch_text.stroke-29"),sQuery(id+"F0.wireOp",EDGE,"E65.sketch_text.stroke-30"),sQuery(id+"F0.wireOp",EDGE,"E65.sketch_text.stroke-31"),sQuery(id+"F0.wireOp",EDGE,"E65.sketch_text.stroke-32"),sQuery(id+"F0.wireOp",EDGE,"E65.sketch_text.stroke-33"),sQuery(id+"F0.wireOp",EDGE,"E65.sketch_text.stroke-34"),sQuery(id+"F0.wireOp",EDGE,"E65.sketch_text.stroke-35"),sQuery(id+"F0.wireOp",EDGE,"E65.sketch_text.stroke-36"),sQuery(id+"F0.wireOp",EDGE,"E65.sketch_text.stroke-37"),sQuery(id+"F0.wireOp",EDGE,"E65.sketch_text.stroke-38"),sQuery(id+"F0.wireOp",EDGE,"E66.sketch_text.stroke-0"),sQuery(id+"F0.wireOp",EDGE,"E66.sketch_text.stroke-1"),sQuery(id+"F0.wireOp",EDGE,"E66.sketch_text.stroke-2"),sQuery(id+"F0.wireOp",EDGE,"E66.sketch_text.stroke-3"),sQuery(id+"F0.wireOp",EDGE,"E66.sketch_text.stroke-4"),sQuery(id+"F0.wireOp",EDGE,"E66.sketch_text.stroke-5"),sQuery(id+"F0.wireOp",EDGE,"E66.sketch_text.stroke-6"),sQuery(id+"F0.wireOp",EDGE,"E66.sketch_text.stroke-7"),sQuery(id+"F0.wireOp",EDGE,"E66.sketch_text.stroke-8"),sQuery(id+"F0.wireOp",EDGE,"E66.sketch_text.stroke-9"),sQuery(id+"F0.wireOp",EDGE,"E66.sketch_text.stroke-10"),sQuery(id+"F0.wireOp",EDGE,"E66.sketch_text.stroke-11"),sQuery(id+"F0.wireOp",EDGE,"E66.sketch_text.stroke-12"),sQuery(id+"F0.wireOp",EDGE,"E66.sketch_text.stroke-13"),sQuery(id+"F0.wireOp",EDGE,"E66.sketch_text.stroke-14"),sQuery(id+"F0.wireOp",EDGE,"E66.sketch_text.stroke-15"),sQuery(id+"F0.wireOp",EDGE,"E66.sketch_text.stroke-16"),sQuery(id+"F0.wireOp",EDGE,"E66.sketch_text.stroke-17"),sQuery(id+"F0.wireOp",EDGE,"E66.sketch_text.stroke-18"),sQuery(id+"F0.wireOp",EDGE,"E66.sketch_text.stroke-19"),sQuery(id+"F0.wireOp",EDGE,"E66.sketch_text.stroke-20"),sQuery(id+"F0.wireOp",EDGE,"E66.sketch_text.stroke-21"),sQuery(id+"F0.wireOp",EDGE,"E66.sketch_text.stroke-22"),sQuery(id+"F0.wireOp",EDGE,"E66.sketch_text.stroke-23"),sQuery(id+"F0.wireOp",EDGE,"E66.sketch_text.stroke-24"),sQuery(id+"F0.wireOp",EDGE,"E66.sketch_text.stroke-25"),sQuery(id+"F0.wireOp",EDGE,"E66.sketch_text.stroke-26"),sQuery(id+"F0.wireOp",EDGE,"E66.sketch_text.stroke-27"),sQuery(id+"F0.wireOp",EDGE,"E66.sketch_text.stroke-28"),sQuery(id+"F0.wireOp",EDGE,"E66.sketch_text.stroke-29"),sQuery(id+"F0.wireOp",EDGE,"E66.sketch_text.stroke-30"),sQuery(id+"F0.wireOp",EDGE,"E66.sketch_text.stroke-31"),sQuery(id+"F0.wireOp",EDGE,"E66.sketch_text.stroke-32"),sQuery(id+"F0.wireOp",EDGE,"E66.sketch_text.stroke-33"),sQuery(id+"F0.wireOp",EDGE,"E66.sketch_text.stroke-34"),sQuery(id+"F0.wireOp",EDGE,"E66.sketch_text.stroke-35"),sQuery(id+"F0.wireOp",EDGE,"E66.sketch_text.stroke-36"),sQuery(id+"F0.wireOp",EDGE,"E66.sketch_text.stroke-37"),sQuery(id+"F0.wireOp",EDGE,"E66.sketch_text.stroke-38"),sQuery(id+"F0.wireOp",EDGE,"E66.sketch_text.stroke-39"),sQuery(id+"F0.wireOp",EDGE,"E66.sketch_text.stroke-40"),sQuery(id+"F0.wireOp",EDGE,"E66.sketch_text.stroke-41"),sQuery(id+"F0.wireOp",EDGE,"E66.sketch_text.stroke-42"),sQuery(id+"F0.wireOp",EDGE,"E66.sketch_text.stroke-43"),sQuery(id+"F0.wireOp",EDGE,"E66.sketch_text.stroke-44"),sQuery(id+"F0.wireOp",EDGE,"E66.sketch_text.stroke-45"),sQuery(id+"F0.wireOp",EDGE,"E66.sketch_text.stroke-46"),sQuery(id+"F0.wireOp",EDGE,"E66.sketch_text.stroke-47"),sQuery(id+"F0.wireOp",EDGE,"E66.sketch_text.stroke-48"),sQuery(id+"F0.wireOp",EDGE,"E66.sketch_text.stroke-49"),sQuery(id+"F0.wireOp",EDGE,"E66.sketch_text.stroke-50"),sQuery(id+"F0.wireOp",EDGE,"E66.sketch_text.stroke-51"),sQuery(id+"F0.wireOp",EDGE,"E66.sketch_text.stroke-52"),sQuery(id+"F0.wireOp",EDGE,"E66.sketch_text.stroke-53"),sQuery(id+"F0.wireOp",EDGE,"E66.sketch_text.stroke-54"),sQuery(id+"F0.wireOp",EDGE,"E66.sketch_text.stroke-55"),sQuery(id+"F0.wireOp",EDGE,"E66.sketch_text.stroke-56"),sQuery(id+"F0.wireOp",EDGE,"E66.sketch_text.stroke-57"),sQuery(id+"F0.wireOp",EDGE,"E66.sketch_text.stroke-58"),sQuery(id+"F0.wireOp",EDGE,"E66.sketch_text.stroke-59"),sQuery(id+"F0.wireOp",EDGE,"E66.sketch_text.stroke-60"),sQuery(id+"F0.wireOp",EDGE,"E66.sketch_text.stroke-61"),sQuery(id+"F0.wireOp",EDGE,"E66.sketch_text.stroke-62"),sQuery(id+"F0.wireOp",EDGE,"E66.sketch_text.stroke-63"),sQuery(id+"F0.wireOp",EDGE,"E66.sketch_text.stroke-64"),sQuery(id+"F0.wireOp",EDGE,"E66.sketch_text.stroke-65"),sQuery(id+"F0.wireOp",EDGE,"E66.sketch_text.stroke-66"),sQuery(id+"F0.wireOp",EDGE,"E66.sketch_text.stroke-67"),sQuery(id+"F0.wireOp",EDGE,"E66.sketch_text.stroke-68")])],"isStart":true}),makeQuery(id+"F1.opExtrude","CAP_FACE",FACE,{"disambiguationData":[OSD([subQ2,sQuery(id+"F0.wireOp",EDGE,"E22.top"),subQ1,subQ0,sQuery(id+"F0.wireOp",EDGE,"E25"),sQuery(id+"F0.wireOp",EDGE,"E28"),sQuery(id+"F0.wireOp",EDGE,"E33.bottom"),sQuery(id+"F0.wireOp",EDGE,"E34.top"),sQuery(id+"F0.wireOp",EDGE,"E42"),sQuery(id+"F0.wireOp",EDGE,"E45"),sQuery(id+"F0.wireOp",EDGE,"E51.sketch_text.stroke-0"),sQuery(id+"F0.wireOp",EDGE,"E51.sketch_text.stroke-1"),sQuery(id+"F0.wireOp",EDGE,"E51.sketch_text.stroke-2"),sQuery(id+"F0.wireOp",EDGE,"E51.sketch_text.stroke-3"),sQuery(id+"F0.wireOp",EDGE,"E51.sketch_text.stroke-4"),sQuery(id+"F0.wireOp",EDGE,"E51.sketch_text.stroke-5"),sQuery(id+"F0.wireOp",EDGE,"E51.sketch_text.stroke-6"),sQuery(id+"F0.wireOp",EDGE,"E51.sketch_text.stroke-7"),sQuery(id+"F0.wireOp",EDGE,"E51.sketch_text.stroke-8"),sQuery(id+"F0.wireOp",EDGE,"E51.sketch_text.stroke-9"),sQuery(id+"F0.wireOp",EDGE,"E51.sketch_text.stroke-10"),sQuery(id+"F0.wireOp",EDGE,"E51.sketch_text.stroke-11"),sQuery(id+"F0.wireOp",EDGE,"E51.sketch_text.stroke-12"),sQuery(id+"F0.wireOp",EDGE,"E51.sketch_text.stroke-13"),sQuery(id+"F0.wireOp",EDGE,"E51.sketch_text.stroke-14"),sQuery(id+"F0.wireOp",EDGE,"E51.sketch_text.stroke-15")])],"isStart":true}),makeQuery(id+"F1.opExtrude","CAP_FACE",FACE,{"disambiguationData":[OSD([sQuery(id+"F0.wireOp",EDGE,"E51.sketch_text.stroke-16"),sQuery(id+"F0.wireOp",EDGE,"E51.sketch_text.stroke-17"),sQuery(id+"F0.wireOp",EDGE,"E51.sketch_text.stroke-18"),sQuery(id+"F0.wireOp",EDGE,"E51.sketch_text.stroke-19"),sQuery(id+"F0.wireOp",EDGE,"E51.sketch_text.stroke-20"),sQuery(id+"F0.wireOp",EDGE,"E51.sketch_text.stroke-21")])],"isStart":true}),makeQuery(id+"F1.opExtrude","CAP_FACE",FACE,{"disambiguationData":[OSD([sQuery(id+"F0.wireOp",EDGE,"E62.sketch_text.stroke-40"),sQuery(id+"F0.wireOp",EDGE,"E62.sketch_text.stroke-41"),sQuery(id+"F0.wireOp",EDGE,"E62.sketch_text.stroke-42"),sQuery(id+"F0.wireOp",EDGE,"E62.sketch_text.stroke-43"),sQuery(id+"F0.wireOp",EDGE,"E62.sketch_text.stroke-44")])],"isStart":true}),makeQuery(id+"F1.opExtrude","CAP_FACE",FACE,{"disambiguationData":[OSD([sQuery(id+"F0.wireOp",EDGE,"E65.sketch_text.stroke-18"),sQuery(id+"F0.wireOp",EDGE,"E65.sketch_text.stroke-19"),sQuery(id+"F0.wireOp",EDGE,"E65.sketch_text.stroke-20"),sQuery(id+"F0.wireOp",EDGE,"E65.sketch_text.stroke-21"),sQuery(id+"F0.wireOp",EDGE,"E65.sketch_text.stroke-22"),sQuery(id+"F0.wireOp",EDGE,"E65.sketch_text.stroke-23"),sQuery(id+"F0.wireOp",EDGE,"E65.sketch_text.stroke-24"),sQuery(id+"F0.wireOp",EDGE,"E65.sketch_text.stroke-25")])],"isStart":true}),makeQuery(id+"F3.opExtrude","CAP_FACE",FACE,{"disambiguationData":[OSD([sQuery(id+"F2.wireOp",EDGE,"E70.bottom"),sQuery(id+"F2.wireOp",EDGE,"E70.top"),sQuery(id+"F2.wireOp",EDGE,"E70.left"),sQuery(id+"F2.wireOp",EDGE,"E70.right")])],"isStart":true})]});}
            var sketch = newSketch(context, id + "F8", { "sketchPlane" : qUnion([Q0])});
            skCircle(sketch, "E87", {"center": v(21.7, 11.5) * mm, "radius": 2.5 * mm});
            skCircle(sketch, "E88", {"center": v(1.7, -11.5) * mm, "radius": 2.5 * mm});
            skCircle(sketch, "E89.0", {"center": v(1.7, 0) * mm, "radius": 0.75 * mm});
            skCircle(sketch, "E90.0", {"center": v(21.7, 0) * mm, "radius": 0.75 * mm});
            skSolve(sketch);
        }
        {
            var Q0;
            Q0 = qSketchRegion(id + "F8", true);
            extrude(context, id + "F9", {"entities" : qUnion([Q0]), "operationType" : NewBodyOperationType.REMOVE, "oppositeDirection" : true, "depth" : 25 * mm});
        }
        {
            var Q0;
            Q0=makeQuery(id+"F1.opExtrude","SWEPT_EDGE",EDGE,{"disambiguationData":[OSD([sQuery(id+"F0.wireOp",EDGE,"E0.top"),sQuery(id+"F0.wireOp",EDGE,"E0.right")])]});
            var Q1;
            Q1=makeQuery(id+"F1.opExtrude","SWEPT_EDGE",EDGE,{"disambiguationData":[OSD([sQuery(id+"F0.wireOp",EDGE,"E0.top"),sQuery(id+"F0.wireOp",EDGE,"E0.left")])]});
            var Q2;
            Q2=makeQuery(id+"F1.opExtrude","SWEPT_EDGE",EDGE,{"disambiguationData":[OSD([sQuery(id+"F0.wireOp",EDGE,"E0.bottom"),sQuery(id+"F0.wireOp",EDGE,"E0.left")])]});
            var Q3;
            Q3=makeQuery(id+"F1.opExtrude","SWEPT_EDGE",EDGE,{"disambiguationData":[OSD([sQuery(id+"F0.wireOp",EDGE,"E0.bottom"),sQuery(id+"F0.wireOp",EDGE,"E0.right")])]});
            fillet(context, id + "F10", {"entities" : qUnion([Q0, Q1, Q2, Q3]), "radius" : 5 * mm, "tangentPropagation" : true, "allowEdgeOverflow" : false});
        }
        {
            var Q0;
            {var subQ0=sQuery(id+"F0.wireOp",EDGE,"E22.right");var subQ1=sQuery(id+"F0.wireOp",EDGE,"E22.left");var subQ2=sQuery(id+"F0.wireOp",EDGE,"E0.left");Q0=makeQuery(id+"F3.boolean.opBoolean","MERGE",FACE,{"derivedFrom":[makeQuery(id+"F1.opExtrude","CAP_FACE",FACE,{"disambiguationData":[OSD([sQuery(id+"F0.wireOp",EDGE,"E0.bottom"),sQuery(id+"F0.wireOp",EDGE,"E0.top"),subQ2,sQuery(id+"F0.wireOp",EDGE,"E0.right"),sQuery(id+"F0.wireOp",EDGE,"E1"),sQuery(id+"F0.wireOp",EDGE,"E2"),sQuery(id+"F0.wireOp",EDGE,"E3"),sQuery(id+"F0.wireOp",EDGE,"E5.bottom"),sQuery(id+"F0.wireOp",EDGE,"E5.top"),sQuery(id+"F0.wireOp",EDGE,"E4"),sQuery(id+"F0.wireOp",EDGE,"E11"),sQuery(id+"F0.wireOp",EDGE,"E12"),sQuery(id+"F0.wireOp",EDGE,"E13"),sQuery(id+"F0.wireOp",EDGE,"E14"),sQuery(id+"F0.wireOp",EDGE,"E15"),sQuery(id+"F0.wireOp",EDGE,"E19"),sQuery(id+"F0.wireOp",EDGE,"E21"),sQuery(id+"F0.wireOp",EDGE,"E22.bottom"),subQ1,subQ0,sQuery(id+"F0.wireOp",EDGE,"E26"),sQuery(id+"F0.wireOp",EDGE,"E27"),sQuery(id+"F0.wireOp",EDGE,"E32.bottom"),sQuery(id+"F0.wireOp",EDGE,"E32.top"),sQuery(id+"F0.wireOp",EDGE,"E32.right"),sQuery(id+"F0.wireOp",EDGE,"E33.top"),sQuery(id+"F0.wireOp",EDGE,"E34.bottom"),sQuery(id+"F0.wireOp",EDGE,"E36"),sQuery(id+"F0.wireOp",EDGE,"E38"),sQuery(id+"F0.wireOp",EDGE,"E40"),sQuery(id+"F0.wireOp",EDGE,"E46"),sQuery(id+"F0.wireOp",EDGE,"E47"),sQuery(id+"F0.wireOp",EDGE,"E50"),sQuery(id+"F0.wireOp",EDGE,"E56.bottom"),sQuery(id+"F0.wireOp",EDGE,"E56.top"),sQuery(id+"F0.wireOp",EDGE,"E57"),sQuery(id+"F0.wireOp",EDGE,"E58"),sQuery(id+"F0.wireOp",EDGE,"E61.sketch_text.stroke-0"),sQuery(id+"F0.wireOp",EDGE,"E61.sketch_text.stroke-1"),sQuery(id+"F0.wireOp",EDGE,"E61.sketch_text.stroke-2"),sQuery(id+"F0.wireOp",EDGE,"E61.sketch_text.stroke-3"),sQuery(id+"F0.wireOp",EDGE,"E61.sketch_text.stroke-4"),sQuery(id+"F0.wireOp",EDGE,"E61.sketch_text.stroke-5"),sQuery(id+"F0.wireOp",EDGE,"E61.sketch_text.stroke-6"),sQuery(id+"F0.wireOp",EDGE,"E61.sketch_text.stroke-7"),sQuery(id+"F0.wireOp",EDGE,"E61.sketch_text.stroke-8"),sQuery(id+"F0.wireOp",EDGE,"E61.sketch_text.stroke-9"),sQuery(id+"F0.wireOp",EDGE,"E61.sketch_text.stroke-10"),sQuery(id+"F0.wireOp",EDGE,"E61.sketch_text.stroke-11"),sQuery(id+"F0.wireOp",EDGE,"E61.sketch_text.stroke-12"),sQuery(id+"F0.wireOp",EDGE,"E61.sketch_text.stroke-13"),sQuery(id+"F0.wireOp",EDGE,"E61.sketch_text.stroke-14"),sQuery(id+"F0.wireOp",EDGE,"E61.sketch_text.stroke-15"),sQuery(id+"F0.wireOp",EDGE,"E61.sketch_text.stroke-16"),sQuery(id+"F0.wireOp",EDGE,"E61.sketch_text.stroke-17"),sQuery(id+"F0.wireOp",EDGE,"E62.sketch_text.stroke-0"),sQuery(id+"F0.wireOp",EDGE,"E62.sketch_text.stroke-1"),sQuery(id+"F0.wireOp",EDGE,"E62.sketch_text.stroke-2"),sQuery(id+"F0.wireOp",EDGE,"E62.sketch_text.stroke-3"),sQuery(id+"F0.wireOp",EDGE,"E62.sketch_text.stroke-4"),sQuery(id+"F0.wireOp",EDGE,"E62.sketch_text.stroke-5"),sQuery(id+"F0.wireOp",EDGE,"E62.sketch_text.stroke-6"),sQuery(id+"F0.wireOp",EDGE,"E62.sketch_text.stroke-7"),sQuery(id+"F0.wireOp",EDGE,"E62.sketch_text.stroke-8"),sQuery(id+"F0.wireOp",EDGE,"E62.sketch_text.stroke-9"),sQuery(id+"F0.wireOp",EDGE,"E62.sketch_text.stroke-10"),sQuery(id+"F0.wireOp",EDGE,"E62.sketch_text.stroke-11"),sQuery(id+"F0.wireOp",EDGE,"E62.sketch_text.stroke-12"),sQuery(id+"F0.wireOp",EDGE,"E62.sketch_text.stroke-13"),sQuery(id+"F0.wireOp",EDGE,"E62.sketch_text.stroke-14"),sQuery(id+"F0.wireOp",EDGE,"E62.sketch_text.stroke-15"),sQuery(id+"F0.wireOp",EDGE,"E62.sketch_text.stroke-16"),sQuery(id+"F0.wireOp",EDGE,"E62.sketch_text.stroke-17"),sQuery(id+"F0.wireOp",EDGE,"E62.sketch_text.stroke-18"),sQuery(id+"F0.wireOp",EDGE,"E62.sketch_text.stroke-19"),sQuery(id+"F0.wireOp",EDGE,"E62.sketch_text.stroke-20"),sQuery(id+"F0.wireOp",EDGE,"E62.sketch_text.stroke-21"),sQuery(id+"F0.wireOp",EDGE,"E62.sketch_text.stroke-22"),sQuery(id+"F0.wireOp",EDGE,"E62.sketch_text.stroke-23"),sQuery(id+"F0.wireOp",EDGE,"E62.sketch_text.stroke-24"),sQuery(id+"F0.wireOp",EDGE,"E62.sketch_text.stroke-25"),sQuery(id+"F0.wireOp",EDGE,"E62.sketch_text.stroke-26"),sQuery(id+"F0.wireOp",EDGE,"E62.sketch_text.stroke-27"),sQuery(id+"F0.wireOp",EDGE,"E62.sketch_text.stroke-28"),sQuery(id+"F0.wireOp",EDGE,"E62.sketch_text.stroke-29"),sQuery(id+"F0.wireOp",EDGE,"E62.sketch_text.stroke-30"),sQuery(id+"F0.wireOp",EDGE,"E62.sketch_text.stroke-31"),sQuery(id+"F0.wireOp",EDGE,"E62.sketch_text.stroke-32"),sQuery(id+"F0.wireOp",EDGE,"E62.sketch_text.stroke-33"),sQuery(id+"F0.wireOp",EDGE,"E62.sketch_text.stroke-34"),sQuery(id+"F0.wireOp",EDGE,"E62.sketch_text.stroke-35"),sQuery(id+"F0.wireOp",EDGE,"E62.sketch_text.stroke-36"),sQuery(id+"F0.wireOp",EDGE,"E62.sketch_text.stroke-37"),sQuery(id+"F0.wireOp",EDGE,"E62.sketch_text.stroke-38"),sQuery(id+"F0.wireOp",EDGE,"E62.sketch_text.stroke-39"),sQuery(id+"F0.wireOp",EDGE,"E63.sketch_text.stroke-0"),sQuery(id+"F0.wireOp",EDGE,"E63.sketch_text.stroke-1"),sQuery(id+"F0.wireOp",EDGE,"E63.sketch_text.stroke-2"),sQuery(id+"F0.wireOp",EDGE,"E63.sketch_text.stroke-3"),sQuery(id+"F0.wireOp",EDGE,"E63.sketch_text.stroke-4"),sQuery(id+"F0.wireOp",EDGE,"E63.sketch_text.stroke-5"),sQuery(id+"F0.wireOp",EDGE,"E63.sketch_text.stroke-6"),sQuery(id+"F0.wireOp",EDGE,"E63.sketch_text.stroke-7"),sQuery(id+"F0.wireOp",EDGE,"E63.sketch_text.stroke-8"),sQuery(id+"F0.wireOp",EDGE,"E63.sketch_text.stroke-9"),sQuery(id+"F0.wireOp",EDGE,"E63.sketch_text.stroke-10"),sQuery(id+"F0.wireOp",EDGE,"E63.sketch_text.stroke-11"),sQuery(id+"F0.wireOp",EDGE,"E63.sketch_text.stroke-12"),sQuery(id+"F0.wireOp",EDGE,"E63.sketch_text.stroke-13"),sQuery(id+"F0.wireOp",EDGE,"E63.sketch_text.stroke-14"),sQuery(id+"F0.wireOp",EDGE,"E63.sketch_text.stroke-15"),sQuery(id+"F0.wireOp",EDGE,"E63.sketch_text.stroke-16"),sQuery(id+"F0.wireOp",EDGE,"E63.sketch_text.stroke-17"),sQuery(id+"F0.wireOp",EDGE,"E63.sketch_text.stroke-18"),sQuery(id+"F0.wireOp",EDGE,"E63.sketch_text.stroke-19"),sQuery(id+"F0.wireOp",EDGE,"E63.sketch_text.stroke-20"),sQuery(id+"F0.wireOp",EDGE,"E63.sketch_text.stroke-21"),sQuery(id+"F0.wireOp",EDGE,"E63.sketch_text.stroke-22"),sQuery(id+"F0.wireOp",EDGE,"E63.sketch_text.stroke-23"),sQuery(id+"F0.wireOp",EDGE,"E63.sketch_text.stroke-24"),sQuery(id+"F0.wireOp",EDGE,"E63.sketch_text.stroke-25"),sQuery(id+"F0.wireOp",EDGE,"E63.sketch_text.stroke-26"),sQuery(id+"F0.wireOp",EDGE,"E63.sketch_text.stroke-27"),sQuery(id+"F0.wireOp",EDGE,"E63.sketch_text.stroke-28"),sQuery(id+"F0.wireOp",EDGE,"E63.sketch_text.stroke-29"),sQuery(id+"F0.wireOp",EDGE,"E63.sketch_text.stroke-30"),sQuery(id+"F0.wireOp",EDGE,"E63.sketch_text.stroke-31"),sQuery(id+"F0.wireOp",EDGE,"E63.sketch_text.stroke-32"),sQuery(id+"F0.wireOp",EDGE,"E63.sketch_text.stroke-33"),sQuery(id+"F0.wireOp",EDGE,"E63.sketch_text.stroke-34"),sQuery(id+"F0.wireOp",EDGE,"E63.sketch_text.stroke-35"),sQuery(id+"F0.wireOp",EDGE,"E63.sketch_text.stroke-36"),sQuery(id+"F0.wireOp",EDGE,"E63.sketch_text.stroke-37"),sQuery(id+"F0.wireOp",EDGE,"E63.sketch_text.stroke-38"),sQuery(id+"F0.wireOp",EDGE,"E63.sketch_text.stroke-39"),sQuery(id+"F0.wireOp",EDGE,"E63.sketch_text.stroke-40"),sQuery(id+"F0.wireOp",EDGE,"E63.sketch_text.stroke-41"),sQuery(id+"F0.wireOp",EDGE,"E63.sketch_text.stroke-42"),sQuery(id+"F0.wireOp",EDGE,"E63.sketch_text.stroke-43"),sQuery(id+"F0.wireOp",EDGE,"E63.sketch_text.stroke-44"),sQuery(id+"F0.wireOp",EDGE,"E63.sketch_text.stroke-45"),sQuery(id+"F0.wireOp",EDGE,"E63.sketch_text.stroke-46"),sQuery(id+"F0.wireOp",EDGE,"E63.sketch_text.stroke-47"),sQuery(id+"F0.wireOp",EDGE,"E63.sketch_text.stroke-48"),sQuery(id+"F0.wireOp",EDGE,"E63.sketch_text.stroke-49"),sQuery(id+"F0.wireOp",EDGE,"E63.sketch_text.stroke-50"),sQuery(id+"F0.wireOp",EDGE,"E63.sketch_text.stroke-51"),sQuery(id+"F0.wireOp",EDGE,"E63.sketch_text.stroke-52"),sQuery(id+"F0.wireOp",EDGE,"E63.sketch_text.stroke-53"),sQuery(id+"F0.wireOp",EDGE,"E63.sketch_text.stroke-54"),sQuery(id+"F0.wireOp",EDGE,"E63.sketch_text.stroke-55"),sQuery(id+"F0.wireOp",EDGE,"E63.sketch_text.stroke-56"),sQuery(id+"F0.wireOp",EDGE,"E63.sketch_text.stroke-57"),sQuery(id+"F0.wireOp",EDGE,"E63.sketch_text.stroke-58"),sQuery(id+"F0.wireOp",EDGE,"E63.sketch_text.stroke-59"),sQuery(id+"F0.wireOp",EDGE,"E63.sketch_text.stroke-60"),sQuery(id+"F0.wireOp",EDGE,"E63.sketch_text.stroke-61"),sQuery(id+"F0.wireOp",EDGE,"E63.sketch_text.stroke-62"),sQuery(id+"F0.wireOp",EDGE,"E63.sketch_text.stroke-63"),sQuery(id+"F0.wireOp",EDGE,"E63.sketch_text.stroke-64"),sQuery(id+"F0.wireOp",EDGE,"E63.sketch_text.stroke-65"),sQuery(id+"F0.wireOp",EDGE,"E63.sketch_text.stroke-66"),sQuery(id+"F0.wireOp",EDGE,"E63.sketch_text.stroke-67"),sQuery(id+"F0.wireOp",EDGE,"E63.sketch_text.stroke-68"),sQuery(id+"F0.wireOp",EDGE,"E63.sketch_text.stroke-69"),sQuery(id+"F0.wireOp",EDGE,"E63.sketch_text.stroke-70"),sQuery(id+"F0.wireOp",EDGE,"E63.sketch_text.stroke-71"),sQuery(id+"F0.wireOp",EDGE,"E63.sketch_text.stroke-72"),sQuery(id+"F0.wireOp",EDGE,"E63.sketch_text.stroke-73"),sQuery(id+"F0.wireOp",EDGE,"E63.sketch_text.stroke-74"),sQuery(id+"F0.wireOp",EDGE,"E63.sketch_text.stroke-75"),sQuery(id+"F0.wireOp",EDGE,"E63.sketch_text.stroke-76"),sQuery(id+"F0.wireOp",EDGE,"E63.sketch_text.stroke-77"),sQuery(id+"F0.wireOp",EDGE,"E63.sketch_text.stroke-78"),sQuery(id+"F0.wireOp",EDGE,"E63.sketch_text.stroke-79"),sQuery(id+"F0.wireOp",EDGE,"E63.sketch_text.stroke-80"),sQuery(id+"F0.wireOp",EDGE,"E63.sketch_text.stroke-81"),sQuery(id+"F0.wireOp",EDGE,"E63.sketch_text.stroke-82"),sQuery(id+"F0.wireOp",EDGE,"E63.sketch_text.stroke-83"),sQuery(id+"F0.wireOp",EDGE,"E63.sketch_text.stroke-84"),sQuery(id+"F0.wireOp",EDGE,"E63.sketch_text.stroke-85"),sQuery(id+"F0.wireOp",EDGE,"E63.sketch_text.stroke-86"),sQuery(id+"F0.wireOp",EDGE,"E63.sketch_text.stroke-87"),sQuery(id+"F0.wireOp",EDGE,"E63.sketch_text.stroke-88"),sQuery(id+"F0.wireOp",EDGE,"E63.sketch_text.stroke-89"),sQuery(id+"F0.wireOp",EDGE,"E63.sketch_text.stroke-90"),sQuery(id+"F0.wireOp",EDGE,"E63.sketch_text.stroke-91"),sQuery(id+"F0.wireOp",EDGE,"E63.sketch_text.stroke-92"),sQuery(id+"F0.wireOp",EDGE,"E63.sketch_text.stroke-93"),sQuery(id+"F0.wireOp",EDGE,"E63.sketch_text.stroke-94"),sQuery(id+"F0.wireOp",EDGE,"E63.sketch_text.stroke-95"),sQuery(id+"F0.wireOp",EDGE,"E63.sketch_text.stroke-96"),sQuery(id+"F0.wireOp",EDGE,"E63.sketch_text.stroke-97"),sQuery(id+"F0.wireOp",EDGE,"E63.sketch_text.stroke-98"),sQuery(id+"F0.wireOp",EDGE,"E63.sketch_text.stroke-99"),sQuery(id+"F0.wireOp",EDGE,"E63.sketch_text.stroke-100"),sQuery(id+"F0.wireOp",EDGE,"E63.sketch_text.stroke-101"),sQuery(id+"F0.wireOp",EDGE,"E63.sketch_text.stroke-102"),sQuery(id+"F0.wireOp",EDGE,"E63.sketch_text.stroke-103"),sQuery(id+"F0.wireOp",EDGE,"E63.sketch_text.stroke-104"),sQuery(id+"F0.wireOp",EDGE,"E63.sketch_text.stroke-105"),sQuery(id+"F0.wireOp",EDGE,"E63.sketch_text.stroke-106"),sQuery(id+"F0.wireOp",EDGE,"E63.sketch_text.stroke-107"),sQuery(id+"F0.wireOp",EDGE,"E63.sketch_text.stroke-108"),sQuery(id+"F0.wireOp",EDGE,"E63.sketch_text.stroke-109"),sQuery(id+"F0.wireOp",EDGE,"E64"),sQuery(id+"F0.wireOp",EDGE,"E65.sketch_text.stroke-0"),sQuery(id+"F0.wireOp",EDGE,"E65.sketch_text.stroke-1"),sQuery(id+"F0.wireOp",EDGE,"E65.sketch_text.stroke-2"),sQuery(id+"F0.wireOp",EDGE,"E65.sketch_text.stroke-3"),sQuery(id+"F0.wireOp",EDGE,"E65.sketch_text.stroke-4"),sQuery(id+"F0.wireOp",EDGE,"E65.sketch_text.stroke-5"),sQuery(id+"F0.wireOp",EDGE,"E65.sketch_text.stroke-6"),sQuery(id+"F0.wireOp",EDGE,"E65.sketch_text.stroke-7"),sQuery(id+"F0.wireOp",EDGE,"E65.sketch_text.stroke-8"),sQuery(id+"F0.wireOp",EDGE,"E65.sketch_text.stroke-9"),sQuery(id+"F0.wireOp",EDGE,"E65.sketch_text.stroke-10"),sQuery(id+"F0.wireOp",EDGE,"E65.sketch_text.stroke-11"),sQuery(id+"F0.wireOp",EDGE,"E65.sketch_text.stroke-12"),sQuery(id+"F0.wireOp",EDGE,"E65.sketch_text.stroke-13"),sQuery(id+"F0.wireOp",EDGE,"E65.sketch_text.stroke-14"),sQuery(id+"F0.wireOp",EDGE,"E65.sketch_text.stroke-15"),sQuery(id+"F0.wireOp",EDGE,"E65.sketch_text.stroke-16"),sQuery(id+"F0.wireOp",EDGE,"E65.sketch_text.stroke-17"),sQuery(id+"F0.wireOp",EDGE,"E65.sketch_text.stroke-26"),sQuery(id+"F0.wireOp",EDGE,"E65.sketch_text.stroke-27"),sQuery(id+"F0.wireOp",EDGE,"E65.sketch_text.stroke-28"),sQuery(id+"F0.wireOp",EDGE,"E65.sketch_text.stroke-29"),sQuery(id+"F0.wireOp",EDGE,"E65.sketch_text.stroke-30"),sQuery(id+"F0.wireOp",EDGE,"E65.sketch_text.stroke-31"),sQuery(id+"F0.wireOp",EDGE,"E65.sketch_text.stroke-32"),sQuery(id+"F0.wireOp",EDGE,"E65.sketch_text.stroke-33"),sQuery(id+"F0.wireOp",EDGE,"E65.sketch_text.stroke-34"),sQuery(id+"F0.wireOp",EDGE,"E65.sketch_text.stroke-35"),sQuery(id+"F0.wireOp",EDGE,"E65.sketch_text.stroke-36"),sQuery(id+"F0.wireOp",EDGE,"E65.sketch_text.stroke-37"),sQuery(id+"F0.wireOp",EDGE,"E65.sketch_text.stroke-38"),sQuery(id+"F0.wireOp",EDGE,"E66.sketch_text.stroke-0"),sQuery(id+"F0.wireOp",EDGE,"E66.sketch_text.stroke-1"),sQuery(id+"F0.wireOp",EDGE,"E66.sketch_text.stroke-2"),sQuery(id+"F0.wireOp",EDGE,"E66.sketch_text.stroke-3"),sQuery(id+"F0.wireOp",EDGE,"E66.sketch_text.stroke-4"),sQuery(id+"F0.wireOp",EDGE,"E66.sketch_text.stroke-5"),sQuery(id+"F0.wireOp",EDGE,"E66.sketch_text.stroke-6"),sQuery(id+"F0.wireOp",EDGE,"E66.sketch_text.stroke-7"),sQuery(id+"F0.wireOp",EDGE,"E66.sketch_text.stroke-8"),sQuery(id+"F0.wireOp",EDGE,"E66.sketch_text.stroke-9"),sQuery(id+"F0.wireOp",EDGE,"E66.sketch_text.stroke-10"),sQuery(id+"F0.wireOp",EDGE,"E66.sketch_text.stroke-11"),sQuery(id+"F0.wireOp",EDGE,"E66.sketch_text.stroke-12"),sQuery(id+"F0.wireOp",EDGE,"E66.sketch_text.stroke-13"),sQuery(id+"F0.wireOp",EDGE,"E66.sketch_text.stroke-14"),sQuery(id+"F0.wireOp",EDGE,"E66.sketch_text.stroke-15"),sQuery(id+"F0.wireOp",EDGE,"E66.sketch_text.stroke-16"),sQuery(id+"F0.wireOp",EDGE,"E66.sketch_text.stroke-17"),sQuery(id+"F0.wireOp",EDGE,"E66.sketch_text.stroke-18"),sQuery(id+"F0.wireOp",EDGE,"E66.sketch_text.stroke-19"),sQuery(id+"F0.wireOp",EDGE,"E66.sketch_text.stroke-20"),sQuery(id+"F0.wireOp",EDGE,"E66.sketch_text.stroke-21"),sQuery(id+"F0.wireOp",EDGE,"E66.sketch_text.stroke-22"),sQuery(id+"F0.wireOp",EDGE,"E66.sketch_text.stroke-23"),sQuery(id+"F0.wireOp",EDGE,"E66.sketch_text.stroke-24"),sQuery(id+"F0.wireOp",EDGE,"E66.sketch_text.stroke-25"),sQuery(id+"F0.wireOp",EDGE,"E66.sketch_text.stroke-26"),sQuery(id+"F0.wireOp",EDGE,"E66.sketch_text.stroke-27"),sQuery(id+"F0.wireOp",EDGE,"E66.sketch_text.stroke-28"),sQuery(id+"F0.wireOp",EDGE,"E66.sketch_text.stroke-29"),sQuery(id+"F0.wireOp",EDGE,"E66.sketch_text.stroke-30"),sQuery(id+"F0.wireOp",EDGE,"E66.sketch_text.stroke-31"),sQuery(id+"F0.wireOp",EDGE,"E66.sketch_text.stroke-32"),sQuery(id+"F0.wireOp",EDGE,"E66.sketch_text.stroke-33"),sQuery(id+"F0.wireOp",EDGE,"E66.sketch_text.stroke-34"),sQuery(id+"F0.wireOp",EDGE,"E66.sketch_text.stroke-35"),sQuery(id+"F0.wireOp",EDGE,"E66.sketch_text.stroke-36"),sQuery(id+"F0.wireOp",EDGE,"E66.sketch_text.stroke-37"),sQuery(id+"F0.wireOp",EDGE,"E66.sketch_text.stroke-38"),sQuery(id+"F0.wireOp",EDGE,"E66.sketch_text.stroke-39"),sQuery(id+"F0.wireOp",EDGE,"E66.sketch_text.stroke-40"),sQuery(id+"F0.wireOp",EDGE,"E66.sketch_text.stroke-41"),sQuery(id+"F0.wireOp",EDGE,"E66.sketch_text.stroke-42"),sQuery(id+"F0.wireOp",EDGE,"E66.sketch_text.stroke-43"),sQuery(id+"F0.wireOp",EDGE,"E66.sketch_text.stroke-44"),sQuery(id+"F0.wireOp",EDGE,"E66.sketch_text.stroke-45"),sQuery(id+"F0.wireOp",EDGE,"E66.sketch_text.stroke-46"),sQuery(id+"F0.wireOp",EDGE,"E66.sketch_text.stroke-47"),sQuery(id+"F0.wireOp",EDGE,"E66.sketch_text.stroke-48"),sQuery(id+"F0.wireOp",EDGE,"E66.sketch_text.stroke-49"),sQuery(id+"F0.wireOp",EDGE,"E66.sketch_text.stroke-50"),sQuery(id+"F0.wireOp",EDGE,"E66.sketch_text.stroke-51"),sQuery(id+"F0.wireOp",EDGE,"E66.sketch_text.stroke-52"),sQuery(id+"F0.wireOp",EDGE,"E66.sketch_text.stroke-53"),sQuery(id+"F0.wireOp",EDGE,"E66.sketch_text.stroke-54"),sQuery(id+"F0.wireOp",EDGE,"E66.sketch_text.stroke-55"),sQuery(id+"F0.wireOp",EDGE,"E66.sketch_text.stroke-56"),sQuery(id+"F0.wireOp",EDGE,"E66.sketch_text.stroke-57"),sQuery(id+"F0.wireOp",EDGE,"E66.sketch_text.stroke-58"),sQuery(id+"F0.wireOp",EDGE,"E66.sketch_text.stroke-59"),sQuery(id+"F0.wireOp",EDGE,"E66.sketch_text.stroke-60"),sQuery(id+"F0.wireOp",EDGE,"E66.sketch_text.stroke-61"),sQuery(id+"F0.wireOp",EDGE,"E66.sketch_text.stroke-62"),sQuery(id+"F0.wireOp",EDGE,"E66.sketch_text.stroke-63"),sQuery(id+"F0.wireOp",EDGE,"E66.sketch_text.stroke-64"),sQuery(id+"F0.wireOp",EDGE,"E66.sketch_text.stroke-65"),sQuery(id+"F0.wireOp",EDGE,"E66.sketch_text.stroke-66"),sQuery(id+"F0.wireOp",EDGE,"E66.sketch_text.stroke-67"),sQuery(id+"F0.wireOp",EDGE,"E66.sketch_text.stroke-68")])],"isStart":true}),makeQuery(id+"F1.opExtrude","CAP_FACE",FACE,{"disambiguationData":[OSD([subQ2,sQuery(id+"F0.wireOp",EDGE,"E22.top"),subQ1,subQ0,sQuery(id+"F0.wireOp",EDGE,"E25"),sQuery(id+"F0.wireOp",EDGE,"E28"),sQuery(id+"F0.wireOp",EDGE,"E33.bottom"),sQuery(id+"F0.wireOp",EDGE,"E34.top"),sQuery(id+"F0.wireOp",EDGE,"E42"),sQuery(id+"F0.wireOp",EDGE,"E45"),sQuery(id+"F0.wireOp",EDGE,"E51.sketch_text.stroke-0"),sQuery(id+"F0.wireOp",EDGE,"E51.sketch_text.stroke-1"),sQuery(id+"F0.wireOp",EDGE,"E51.sketch_text.stroke-2"),sQuery(id+"F0.wireOp",EDGE,"E51.sketch_text.stroke-3"),sQuery(id+"F0.wireOp",EDGE,"E51.sketch_text.stroke-4"),sQuery(id+"F0.wireOp",EDGE,"E51.sketch_text.stroke-5"),sQuery(id+"F0.wireOp",EDGE,"E51.sketch_text.stroke-6"),sQuery(id+"F0.wireOp",EDGE,"E51.sketch_text.stroke-7"),sQuery(id+"F0.wireOp",EDGE,"E51.sketch_text.stroke-8"),sQuery(id+"F0.wireOp",EDGE,"E51.sketch_text.stroke-9"),sQuery(id+"F0.wireOp",EDGE,"E51.sketch_text.stroke-10"),sQuery(id+"F0.wireOp",EDGE,"E51.sketch_text.stroke-11"),sQuery(id+"F0.wireOp",EDGE,"E51.sketch_text.stroke-12"),sQuery(id+"F0.wireOp",EDGE,"E51.sketch_text.stroke-13"),sQuery(id+"F0.wireOp",EDGE,"E51.sketch_text.stroke-14"),sQuery(id+"F0.wireOp",EDGE,"E51.sketch_text.stroke-15")])],"isStart":true}),makeQuery(id+"F1.opExtrude","CAP_FACE",FACE,{"disambiguationData":[OSD([sQuery(id+"F0.wireOp",EDGE,"E51.sketch_text.stroke-16"),sQuery(id+"F0.wireOp",EDGE,"E51.sketch_text.stroke-17"),sQuery(id+"F0.wireOp",EDGE,"E51.sketch_text.stroke-18"),sQuery(id+"F0.wireOp",EDGE,"E51.sketch_text.stroke-19"),sQuery(id+"F0.wireOp",EDGE,"E51.sketch_text.stroke-20"),sQuery(id+"F0.wireOp",EDGE,"E51.sketch_text.stroke-21")])],"isStart":true}),makeQuery(id+"F1.opExtrude","CAP_FACE",FACE,{"disambiguationData":[OSD([sQuery(id+"F0.wireOp",EDGE,"E62.sketch_text.stroke-40"),sQuery(id+"F0.wireOp",EDGE,"E62.sketch_text.stroke-41"),sQuery(id+"F0.wireOp",EDGE,"E62.sketch_text.stroke-42"),sQuery(id+"F0.wireOp",EDGE,"E62.sketch_text.stroke-43"),sQuery(id+"F0.wireOp",EDGE,"E62.sketch_text.stroke-44")])],"isStart":true}),makeQuery(id+"F1.opExtrude","CAP_FACE",FACE,{"disambiguationData":[OSD([sQuery(id+"F0.wireOp",EDGE,"E65.sketch_text.stroke-18"),sQuery(id+"F0.wireOp",EDGE,"E65.sketch_text.stroke-19"),sQuery(id+"F0.wireOp",EDGE,"E65.sketch_text.stroke-20"),sQuery(id+"F0.wireOp",EDGE,"E65.sketch_text.stroke-21"),sQuery(id+"F0.wireOp",EDGE,"E65.sketch_text.stroke-22"),sQuery(id+"F0.wireOp",EDGE,"E65.sketch_text.stroke-23"),sQuery(id+"F0.wireOp",EDGE,"E65.sketch_text.stroke-24"),sQuery(id+"F0.wireOp",EDGE,"E65.sketch_text.stroke-25")])],"isStart":true}),makeQuery(id+"F3.opExtrude","CAP_FACE",FACE,{"disambiguationData":[OSD([sQuery(id+"F2.wireOp",EDGE,"E70.bottom"),sQuery(id+"F2.wireOp",EDGE,"E70.top"),sQuery(id+"F2.wireOp",EDGE,"E70.left"),sQuery(id+"F2.wireOp",EDGE,"E70.right")])],"isStart":true})]});}
            var sketch = newSketch(context, id + "F11", { "sketchPlane" : qUnion([Q0])});
            skText(sketch, "E91", { "text": "ACTIVE LOW", "fontName": "OpenSans-Bold.ttf"});
            const initialGuessF11  = {"E91": [-0.0093, 0.0105, 1, 0, 0.003]};
            skSetInitialGuess(sketch, initialGuessF11);
            skSolve(sketch);
        }
        {
            var Q0;
            Q0 = qSketchRegion(id + "F11", true);
            extrude(context, id + "F12", {"entities" : qUnion([Q0]), "operationType" : NewBodyOperationType.REMOVE, "oppositeDirection" : true, "depth" : 0.6 * mm});
        }
        {
            var Q0;
            {var subQ0=sQuery(id+"F0.wireOp",EDGE,"E19");Q0=makeQuery(id+"F1.opExtrude","SWEPT_FACE",FACE,{"disambiguationData":[OSD([subQ0]),TDD([makeQuery(id+"F0.imprint","IMPRINT",EDGE,{"disambiguationData":[TD([[makeQuery(id+"F0.imprint","INTERSECT",VERTEX,{"derivedFrom":[sQuery(id+"F0.wireOp",EDGE,"E2"),subQ0]}),-1.0]])],"derivedFrom":subQ0})])]});}
            var Q1;
            {var subQ0=sQuery(id+"F0.wireOp",EDGE,"E21");Q1=makeQuery(id+"F1.opExtrude","SWEPT_FACE",FACE,{"disambiguationData":[OSD([subQ0]),TDD([makeQuery(id+"F0.imprint","IMPRINT",EDGE,{"disambiguationData":[TD([[makeQuery(id+"F0.imprint","INTERSECT",VERTEX,{"derivedFrom":[sQuery(id+"F0.wireOp",EDGE,"E2"),subQ0]}),1.0]])],"derivedFrom":subQ0})])]});}
            cPlane(context, id + "F13", {"entities" : qUnion([Q0, Q1]), "cplaneType" : CPlaneType.MID_PLANE, "offset" : 25 * mm, "width" : 150 * mm, "height" : 150 * mm});
        }
        {
            var Q0;
            {var subQ0=sQuery(id+"F0.wireOp",EDGE,"E26");var subQ1=sQuery(id+"F0.wireOp",EDGE,"E3");Q0=makeQuery(id+"F3.boolean.opBoolean","INTERSECT",VERTEX,{"derivedFrom":[makeQuery(id+"F1.opExtrude","SWEPT_FACE",FACE,{"disambiguationData":[OSD([subQ1])]}),makeQuery(id+"F1.opExtrude","SWEPT_FACE",FACE,{"disambiguationData":[OSD([subQ0]),TDD([makeQuery(id+"F0.imprint","IMPRINT",EDGE,{"disambiguationData":[TD([[makeQuery(id+"F0.imprint","INTERSECT",VERTEX,{"derivedFrom":[sQuery(id+"F0.wireOp",EDGE,"E22.right"),subQ0]}),1.0]])],"derivedFrom":subQ0})])]}),makeQuery(id+"F3.opExtrude","CAP_FACE",FACE,{"disambiguationData":[OSD([sQuery(id+"F2.wireOp",EDGE,"E70.bottom"),sQuery(id+"F2.wireOp",EDGE,"E70.top"),sQuery(id+"F2.wireOp",EDGE,"E70.left"),sQuery(id+"F2.wireOp",EDGE,"E70.right")])],"isStart":false})]});}
            var Q1;
            Q1=makeQuery(id+"F1.opExtrude","CAP_VERTEX",VERTEX,{"disambiguationData":[OSD([sQuery(id+"F0.wireOp",EDGE,"E3"),sQuery(id+"F0.wireOp",EDGE,"E24"),sQuery(id+"F0.wireOp",EDGE,"E26")])],"isStart":false});
            var Q2;
            {var subQ0=sQuery(id+"F0.wireOp",EDGE,"E19");var subQ1=sQuery(id+"F0.wireOp",EDGE,"E2");Q2=makeQuery(id+"F3.boolean.opBoolean","INTERSECT",VERTEX,{"derivedFrom":[makeQuery(id+"F1.opExtrude","SWEPT_FACE",FACE,{"disambiguationData":[OSD([subQ1])]}),makeQuery(id+"F1.opExtrude","SWEPT_FACE",FACE,{"disambiguationData":[OSD([subQ0]),TDD([makeQuery(id+"F0.imprint","IMPRINT",EDGE,{"disambiguationData":[TD([[makeQuery(id+"F0.imprint","INTERSECT",VERTEX,{"derivedFrom":[subQ1,subQ0]}),-1.0]])],"derivedFrom":subQ0})])]}),makeQuery(id+"F3.opExtrude","CAP_FACE",FACE,{"disambiguationData":[OSD([sQuery(id+"F2.wireOp",EDGE,"E70.bottom"),sQuery(id+"F2.wireOp",EDGE,"E70.top"),sQuery(id+"F2.wireOp",EDGE,"E70.left"),sQuery(id+"F2.wireOp",EDGE,"E70.right")])],"isStart":false})]});}
            cPlane(context, id + "F14", {"entities" : qUnion([Q0, Q1, Q2]), "cplaneType" : CPlaneType.THREE_POINT, "offset" : 25 * mm, "width" : 150 * mm, "height" : 150 * mm});
        }
        {
            var Q0;
            Q0=qCreatedBy(id+"F14.planeOp",FACE);
            var sketch = newSketch(context, id + "F15", { "sketchPlane" : qUnion([Q0])});
            skLineSegment(sketch, "E92.0", {"start": v(-3.25, 5.5) * mm, "end": v(-3.25, 3) * mm});
            skLineSegment(sketch, "E93", {"start": v(-3.25, 3) * mm, "end": v(-2.25, 5.5) * mm});
            skLineSegment(sketch, "E94", {"start": v(-2.25, 5.5) * mm, "end": v(-3.25, 5.5) * mm});
            skSolve(sketch);
        }
        {
            var Q0;
            Q0 = qSketchRegion(id + "F15", true);
            var Q1;
            Q1=sQuery(id+"F15.wireOp",EDGE,"E92.0");
            revolve(context, id + "F16", {"operationType" : NewBodyOperationType.REMOVE, "entities" : qUnion([Q0]), "axis" : qUnion([Q1]), "revolveType" : RevolveType.FULL, "oppositeDirection" : true});
        }
        {
            var Q0;
            Q0=makeQuery(id+"F1.opExtrude","CAP_FACE",FACE,{"disambiguationData":[OSD([sQuery(id+"F0.wireOp",EDGE,"E0.bottom"),sQuery(id+"F0.wireOp",EDGE,"E0.top"),sQuery(id+"F0.wireOp",EDGE,"E0.left"),sQuery(id+"F0.wireOp",EDGE,"E0.right"),sQuery(id+"F0.wireOp",EDGE,"E1"),sQuery(id+"F0.wireOp",EDGE,"E2"),sQuery(id+"F0.wireOp",EDGE,"E3"),sQuery(id+"F0.wireOp",EDGE,"E5.bottom"),sQuery(id+"F0.wireOp",EDGE,"E5.top"),sQuery(id+"F0.wireOp",EDGE,"E4"),sQuery(id+"F0.wireOp",EDGE,"E11"),sQuery(id+"F0.wireOp",EDGE,"E12"),sQuery(id+"F0.wireOp",EDGE,"E13"),sQuery(id+"F0.wireOp",EDGE,"E14"),sQuery(id+"F0.wireOp",EDGE,"E15"),sQuery(id+"F0.wireOp",EDGE,"E19"),sQuery(id+"F0.wireOp",EDGE,"E21"),sQuery(id+"F0.wireOp",EDGE,"E22.bottom"),sQuery(id+"F0.wireOp",EDGE,"E22.left"),sQuery(id+"F0.wireOp",EDGE,"E22.right"),sQuery(id+"F0.wireOp",EDGE,"E26"),sQuery(id+"F0.wireOp",EDGE,"E27"),sQuery(id+"F0.wireOp",EDGE,"E32.bottom"),sQuery(id+"F0.wireOp",EDGE,"E32.top"),sQuery(id+"F0.wireOp",EDGE,"E32.right"),sQuery(id+"F0.wireOp",EDGE,"E33.top"),sQuery(id+"F0.wireOp",EDGE,"E34.bottom"),sQuery(id+"F0.wireOp",EDGE,"E36"),sQuery(id+"F0.wireOp",EDGE,"E38"),sQuery(id+"F0.wireOp",EDGE,"E40"),sQuery(id+"F0.wireOp",EDGE,"E46"),sQuery(id+"F0.wireOp",EDGE,"E47"),sQuery(id+"F0.wireOp",EDGE,"E50"),sQuery(id+"F0.wireOp",EDGE,"E56.bottom"),sQuery(id+"F0.wireOp",EDGE,"E56.top"),sQuery(id+"F0.wireOp",EDGE,"E57"),sQuery(id+"F0.wireOp",EDGE,"E58"),sQuery(id+"F0.wireOp",EDGE,"E61.sketch_text.stroke-0"),sQuery(id+"F0.wireOp",EDGE,"E61.sketch_text.stroke-1"),sQuery(id+"F0.wireOp",EDGE,"E61.sketch_text.stroke-2"),sQuery(id+"F0.wireOp",EDGE,"E61.sketch_text.stroke-3"),sQuery(id+"F0.wireOp",EDGE,"E61.sketch_text.stroke-4"),sQuery(id+"F0.wireOp",EDGE,"E61.sketch_text.stroke-5"),sQuery(id+"F0.wireOp",EDGE,"E61.sketch_text.stroke-6"),sQuery(id+"F0.wireOp",EDGE,"E61.sketch_text.stroke-7"),sQuery(id+"F0.wireOp",EDGE,"E61.sketch_text.stroke-8"),sQuery(id+"F0.wireOp",EDGE,"E61.sketch_text.stroke-9"),sQuery(id+"F0.wireOp",EDGE,"E61.sketch_text.stroke-10"),sQuery(id+"F0.wireOp",EDGE,"E61.sketch_text.stroke-11"),sQuery(id+"F0.wireOp",EDGE,"E61.sketch_text.stroke-12"),sQuery(id+"F0.wireOp",EDGE,"E61.sketch_text.stroke-13"),sQuery(id+"F0.wireOp",EDGE,"E61.sketch_text.stroke-14"),sQuery(id+"F0.wireOp",EDGE,"E61.sketch_text.stroke-15"),sQuery(id+"F0.wireOp",EDGE,"E61.sketch_text.stroke-16"),sQuery(id+"F0.wireOp",EDGE,"E61.sketch_text.stroke-17"),sQuery(id+"F0.wireOp",EDGE,"E62.sketch_text.stroke-0"),sQuery(id+"F0.wireOp",EDGE,"E62.sketch_text.stroke-1"),sQuery(id+"F0.wireOp",EDGE,"E62.sketch_text.stroke-2"),sQuery(id+"F0.wireOp",EDGE,"E62.sketch_text.stroke-3"),sQuery(id+"F0.wireOp",EDGE,"E62.sketch_text.stroke-4"),sQuery(id+"F0.wireOp",EDGE,"E62.sketch_text.stroke-5"),sQuery(id+"F0.wireOp",EDGE,"E62.sketch_text.stroke-6"),sQuery(id+"F0.wireOp",EDGE,"E62.sketch_text.stroke-7"),sQuery(id+"F0.wireOp",EDGE,"E62.sketch_text.stroke-8"),sQuery(id+"F0.wireOp",EDGE,"E62.sketch_text.stroke-9"),sQuery(id+"F0.wireOp",EDGE,"E62.sketch_text.stroke-10"),sQuery(id+"F0.wireOp",EDGE,"E62.sketch_text.stroke-11"),sQuery(id+"F0.wireOp",EDGE,"E62.sketch_text.stroke-12"),sQuery(id+"F0.wireOp",EDGE,"E62.sketch_text.stroke-13"),sQuery(id+"F0.wireOp",EDGE,"E62.sketch_text.stroke-14"),sQuery(id+"F0.wireOp",EDGE,"E62.sketch_text.stroke-15"),sQuery(id+"F0.wireOp",EDGE,"E62.sketch_text.stroke-16"),sQuery(id+"F0.wireOp",EDGE,"E62.sketch_text.stroke-17"),sQuery(id+"F0.wireOp",EDGE,"E62.sketch_text.stroke-18"),sQuery(id+"F0.wireOp",EDGE,"E62.sketch_text.stroke-19"),sQuery(id+"F0.wireOp",EDGE,"E62.sketch_text.stroke-20"),sQuery(id+"F0.wireOp",EDGE,"E62.sketch_text.stroke-21"),sQuery(id+"F0.wireOp",EDGE,"E62.sketch_text.stroke-22"),sQuery(id+"F0.wireOp",EDGE,"E62.sketch_text.stroke-23"),sQuery(id+"F0.wireOp",EDGE,"E62.sketch_text.stroke-24"),sQuery(id+"F0.wireOp",EDGE,"E62.sketch_text.stroke-25"),sQuery(id+"F0.wireOp",EDGE,"E62.sketch_text.stroke-26"),sQuery(id+"F0.wireOp",EDGE,"E62.sketch_text.stroke-27"),sQuery(id+"F0.wireOp",EDGE,"E62.sketch_text.stroke-28"),sQuery(id+"F0.wireOp",EDGE,"E62.sketch_text.stroke-29"),sQuery(id+"F0.wireOp",EDGE,"E62.sketch_text.stroke-30"),sQuery(id+"F0.wireOp",EDGE,"E62.sketch_text.stroke-31"),sQuery(id+"F0.wireOp",EDGE,"E62.sketch_text.stroke-32"),sQuery(id+"F0.wireOp",EDGE,"E62.sketch_text.stroke-33"),sQuery(id+"F0.wireOp",EDGE,"E62.sketch_text.stroke-34"),sQuery(id+"F0.wireOp",EDGE,"E62.sketch_text.stroke-35"),sQuery(id+"F0.wireOp",EDGE,"E62.sketch_text.stroke-36"),sQuery(id+"F0.wireOp",EDGE,"E62.sketch_text.stroke-37"),sQuery(id+"F0.wireOp",EDGE,"E62.sketch_text.stroke-38"),sQuery(id+"F0.wireOp",EDGE,"E62.sketch_text.stroke-39"),sQuery(id+"F0.wireOp",EDGE,"E63.sketch_text.stroke-0"),sQuery(id+"F0.wireOp",EDGE,"E63.sketch_text.stroke-1"),sQuery(id+"F0.wireOp",EDGE,"E63.sketch_text.stroke-2"),sQuery(id+"F0.wireOp",EDGE,"E63.sketch_text.stroke-3"),sQuery(id+"F0.wireOp",EDGE,"E63.sketch_text.stroke-4"),sQuery(id+"F0.wireOp",EDGE,"E63.sketch_text.stroke-5"),sQuery(id+"F0.wireOp",EDGE,"E63.sketch_text.stroke-6"),sQuery(id+"F0.wireOp",EDGE,"E63.sketch_text.stroke-7"),sQuery(id+"F0.wireOp",EDGE,"E63.sketch_text.stroke-8"),sQuery(id+"F0.wireOp",EDGE,"E63.sketch_text.stroke-9"),sQuery(id+"F0.wireOp",EDGE,"E63.sketch_text.stroke-10"),sQuery(id+"F0.wireOp",EDGE,"E63.sketch_text.stroke-11"),sQuery(id+"F0.wireOp",EDGE,"E63.sketch_text.stroke-12"),sQuery(id+"F0.wireOp",EDGE,"E63.sketch_text.stroke-13"),sQuery(id+"F0.wireOp",EDGE,"E63.sketch_text.stroke-14"),sQuery(id+"F0.wireOp",EDGE,"E63.sketch_text.stroke-15"),sQuery(id+"F0.wireOp",EDGE,"E63.sketch_text.stroke-16"),sQuery(id+"F0.wireOp",EDGE,"E63.sketch_text.stroke-17"),sQuery(id+"F0.wireOp",EDGE,"E63.sketch_text.stroke-18"),sQuery(id+"F0.wireOp",EDGE,"E63.sketch_text.stroke-19"),sQuery(id+"F0.wireOp",EDGE,"E63.sketch_text.stroke-20"),sQuery(id+"F0.wireOp",EDGE,"E63.sketch_text.stroke-21"),sQuery(id+"F0.wireOp",EDGE,"E63.sketch_text.stroke-22"),sQuery(id+"F0.wireOp",EDGE,"E63.sketch_text.stroke-23"),sQuery(id+"F0.wireOp",EDGE,"E63.sketch_text.stroke-24"),sQuery(id+"F0.wireOp",EDGE,"E63.sketch_text.stroke-25"),sQuery(id+"F0.wireOp",EDGE,"E63.sketch_text.stroke-26"),sQuery(id+"F0.wireOp",EDGE,"E63.sketch_text.stroke-27"),sQuery(id+"F0.wireOp",EDGE,"E63.sketch_text.stroke-28"),sQuery(id+"F0.wireOp",EDGE,"E63.sketch_text.stroke-29"),sQuery(id+"F0.wireOp",EDGE,"E63.sketch_text.stroke-30"),sQuery(id+"F0.wireOp",EDGE,"E63.sketch_text.stroke-31"),sQuery(id+"F0.wireOp",EDGE,"E63.sketch_text.stroke-32"),sQuery(id+"F0.wireOp",EDGE,"E63.sketch_text.stroke-33"),sQuery(id+"F0.wireOp",EDGE,"E63.sketch_text.stroke-34"),sQuery(id+"F0.wireOp",EDGE,"E63.sketch_text.stroke-35"),sQuery(id+"F0.wireOp",EDGE,"E63.sketch_text.stroke-36"),sQuery(id+"F0.wireOp",EDGE,"E63.sketch_text.stroke-37"),sQuery(id+"F0.wireOp",EDGE,"E63.sketch_text.stroke-38"),sQuery(id+"F0.wireOp",EDGE,"E63.sketch_text.stroke-39"),sQuery(id+"F0.wireOp",EDGE,"E63.sketch_text.stroke-40"),sQuery(id+"F0.wireOp",EDGE,"E63.sketch_text.stroke-41"),sQuery(id+"F0.wireOp",EDGE,"E63.sketch_text.stroke-42"),sQuery(id+"F0.wireOp",EDGE,"E63.sketch_text.stroke-43"),sQuery(id+"F0.wireOp",EDGE,"E63.sketch_text.stroke-44"),sQuery(id+"F0.wireOp",EDGE,"E63.sketch_text.stroke-45"),sQuery(id+"F0.wireOp",EDGE,"E63.sketch_text.stroke-46"),sQuery(id+"F0.wireOp",EDGE,"E63.sketch_text.stroke-47"),sQuery(id+"F0.wireOp",EDGE,"E63.sketch_text.stroke-48"),sQuery(id+"F0.wireOp",EDGE,"E63.sketch_text.stroke-49"),sQuery(id+"F0.wireOp",EDGE,"E63.sketch_text.stroke-50"),sQuery(id+"F0.wireOp",EDGE,"E63.sketch_text.stroke-51"),sQuery(id+"F0.wireOp",EDGE,"E63.sketch_text.stroke-52"),sQuery(id+"F0.wireOp",EDGE,"E63.sketch_text.stroke-53"),sQuery(id+"F0.wireOp",EDGE,"E63.sketch_text.stroke-54"),sQuery(id+"F0.wireOp",EDGE,"E63.sketch_text.stroke-55"),sQuery(id+"F0.wireOp",EDGE,"E63.sketch_text.stroke-56"),sQuery(id+"F0.wireOp",EDGE,"E63.sketch_text.stroke-57"),sQuery(id+"F0.wireOp",EDGE,"E63.sketch_text.stroke-58"),sQuery(id+"F0.wireOp",EDGE,"E63.sketch_text.stroke-59"),sQuery(id+"F0.wireOp",EDGE,"E63.sketch_text.stroke-60"),sQuery(id+"F0.wireOp",EDGE,"E63.sketch_text.stroke-61"),sQuery(id+"F0.wireOp",EDGE,"E63.sketch_text.stroke-62"),sQuery(id+"F0.wireOp",EDGE,"E63.sketch_text.stroke-63"),sQuery(id+"F0.wireOp",EDGE,"E63.sketch_text.stroke-64"),sQuery(id+"F0.wireOp",EDGE,"E63.sketch_text.stroke-65"),sQuery(id+"F0.wireOp",EDGE,"E63.sketch_text.stroke-66"),sQuery(id+"F0.wireOp",EDGE,"E63.sketch_text.stroke-67"),sQuery(id+"F0.wireOp",EDGE,"E63.sketch_text.stroke-68"),sQuery(id+"F0.wireOp",EDGE,"E63.sketch_text.stroke-69"),sQuery(id+"F0.wireOp",EDGE,"E63.sketch_text.stroke-70"),sQuery(id+"F0.wireOp",EDGE,"E63.sketch_text.stroke-71"),sQuery(id+"F0.wireOp",EDGE,"E63.sketch_text.stroke-72"),sQuery(id+"F0.wireOp",EDGE,"E63.sketch_text.stroke-73"),sQuery(id+"F0.wireOp",EDGE,"E63.sketch_text.stroke-74"),sQuery(id+"F0.wireOp",EDGE,"E63.sketch_text.stroke-75"),sQuery(id+"F0.wireOp",EDGE,"E63.sketch_text.stroke-76"),sQuery(id+"F0.wireOp",EDGE,"E63.sketch_text.stroke-77"),sQuery(id+"F0.wireOp",EDGE,"E63.sketch_text.stroke-78"),sQuery(id+"F0.wireOp",EDGE,"E63.sketch_text.stroke-79"),sQuery(id+"F0.wireOp",EDGE,"E63.sketch_text.stroke-80"),sQuery(id+"F0.wireOp",EDGE,"E63.sketch_text.stroke-81"),sQuery(id+"F0.wireOp",EDGE,"E63.sketch_text.stroke-82"),sQuery(id+"F0.wireOp",EDGE,"E63.sketch_text.stroke-83"),sQuery(id+"F0.wireOp",EDGE,"E63.sketch_text.stroke-84"),sQuery(id+"F0.wireOp",EDGE,"E63.sketch_text.stroke-85"),sQuery(id+"F0.wireOp",EDGE,"E63.sketch_text.stroke-86"),sQuery(id+"F0.wireOp",EDGE,"E63.sketch_text.stroke-87"),sQuery(id+"F0.wireOp",EDGE,"E63.sketch_text.stroke-88"),sQuery(id+"F0.wireOp",EDGE,"E63.sketch_text.stroke-89"),sQuery(id+"F0.wireOp",EDGE,"E63.sketch_text.stroke-90"),sQuery(id+"F0.wireOp",EDGE,"E63.sketch_text.stroke-91"),sQuery(id+"F0.wireOp",EDGE,"E63.sketch_text.stroke-92"),sQuery(id+"F0.wireOp",EDGE,"E63.sketch_text.stroke-93"),sQuery(id+"F0.wireOp",EDGE,"E63.sketch_text.stroke-94"),sQuery(id+"F0.wireOp",EDGE,"E63.sketch_text.stroke-95"),sQuery(id+"F0.wireOp",EDGE,"E63.sketch_text.stroke-96"),sQuery(id+"F0.wireOp",EDGE,"E63.sketch_text.stroke-97"),sQuery(id+"F0.wireOp",EDGE,"E63.sketch_text.stroke-98"),sQuery(id+"F0.wireOp",EDGE,"E63.sketch_text.stroke-99"),sQuery(id+"F0.wireOp",EDGE,"E63.sketch_text.stroke-100"),sQuery(id+"F0.wireOp",EDGE,"E63.sketch_text.stroke-101"),sQuery(id+"F0.wireOp",EDGE,"E63.sketch_text.stroke-102"),sQuery(id+"F0.wireOp",EDGE,"E63.sketch_text.stroke-103"),sQuery(id+"F0.wireOp",EDGE,"E63.sketch_text.stroke-104"),sQuery(id+"F0.wireOp",EDGE,"E63.sketch_text.stroke-105"),sQuery(id+"F0.wireOp",EDGE,"E63.sketch_text.stroke-106"),sQuery(id+"F0.wireOp",EDGE,"E63.sketch_text.stroke-107"),sQuery(id+"F0.wireOp",EDGE,"E63.sketch_text.stroke-108"),sQuery(id+"F0.wireOp",EDGE,"E63.sketch_text.stroke-109"),sQuery(id+"F0.wireOp",EDGE,"E64"),sQuery(id+"F0.wireOp",EDGE,"E65.sketch_text.stroke-0"),sQuery(id+"F0.wireOp",EDGE,"E65.sketch_text.stroke-1"),sQuery(id+"F0.wireOp",EDGE,"E65.sketch_text.stroke-2"),sQuery(id+"F0.wireOp",EDGE,"E65.sketch_text.stroke-3"),sQuery(id+"F0.wireOp",EDGE,"E65.sketch_text.stroke-4"),sQuery(id+"F0.wireOp",EDGE,"E65.sketch_text.stroke-5"),sQuery(id+"F0.wireOp",EDGE,"E65.sketch_text.stroke-6"),sQuery(id+"F0.wireOp",EDGE,"E65.sketch_text.stroke-7"),sQuery(id+"F0.wireOp",EDGE,"E65.sketch_text.stroke-8"),sQuery(id+"F0.wireOp",EDGE,"E65.sketch_text.stroke-9"),sQuery(id+"F0.wireOp",EDGE,"E65.sketch_text.stroke-10"),sQuery(id+"F0.wireOp",EDGE,"E65.sketch_text.stroke-11"),sQuery(id+"F0.wireOp",EDGE,"E65.sketch_text.stroke-12"),sQuery(id+"F0.wireOp",EDGE,"E65.sketch_text.stroke-13"),sQuery(id+"F0.wireOp",EDGE,"E65.sketch_text.stroke-14"),sQuery(id+"F0.wireOp",EDGE,"E65.sketch_text.stroke-15"),sQuery(id+"F0.wireOp",EDGE,"E65.sketch_text.stroke-16"),sQuery(id+"F0.wireOp",EDGE,"E65.sketch_text.stroke-17"),sQuery(id+"F0.wireOp",EDGE,"E65.sketch_text.stroke-26"),sQuery(id+"F0.wireOp",EDGE,"E65.sketch_text.stroke-27"),sQuery(id+"F0.wireOp",EDGE,"E65.sketch_text.stroke-28"),sQuery(id+"F0.wireOp",EDGE,"E65.sketch_text.stroke-29"),sQuery(id+"F0.wireOp",EDGE,"E65.sketch_text.stroke-30"),sQuery(id+"F0.wireOp",EDGE,"E65.sketch_text.stroke-31"),sQuery(id+"F0.wireOp",EDGE,"E65.sketch_text.stroke-32"),sQuery(id+"F0.wireOp",EDGE,"E65.sketch_text.stroke-33"),sQuery(id+"F0.wireOp",EDGE,"E65.sketch_text.stroke-34"),sQuery(id+"F0.wireOp",EDGE,"E65.sketch_text.stroke-35"),sQuery(id+"F0.wireOp",EDGE,"E65.sketch_text.stroke-36"),sQuery(id+"F0.wireOp",EDGE,"E65.sketch_text.stroke-37"),sQuery(id+"F0.wireOp",EDGE,"E65.sketch_text.stroke-38"),sQuery(id+"F0.wireOp",EDGE,"E66.sketch_text.stroke-0"),sQuery(id+"F0.wireOp",EDGE,"E66.sketch_text.stroke-1"),sQuery(id+"F0.wireOp",EDGE,"E66.sketch_text.stroke-2"),sQuery(id+"F0.wireOp",EDGE,"E66.sketch_text.stroke-3"),sQuery(id+"F0.wireOp",EDGE,"E66.sketch_text.stroke-4"),sQuery(id+"F0.wireOp",EDGE,"E66.sketch_text.stroke-5"),sQuery(id+"F0.wireOp",EDGE,"E66.sketch_text.stroke-6"),sQuery(id+"F0.wireOp",EDGE,"E66.sketch_text.stroke-7"),sQuery(id+"F0.wireOp",EDGE,"E66.sketch_text.stroke-8"),sQuery(id+"F0.wireOp",EDGE,"E66.sketch_text.stroke-9"),sQuery(id+"F0.wireOp",EDGE,"E66.sketch_text.stroke-10"),sQuery(id+"F0.wireOp",EDGE,"E66.sketch_text.stroke-11"),sQuery(id+"F0.wireOp",EDGE,"E66.sketch_text.stroke-12"),sQuery(id+"F0.wireOp",EDGE,"E66.sketch_text.stroke-13"),sQuery(id+"F0.wireOp",EDGE,"E66.sketch_text.stroke-14"),sQuery(id+"F0.wireOp",EDGE,"E66.sketch_text.stroke-15"),sQuery(id+"F0.wireOp",EDGE,"E66.sketch_text.stroke-16"),sQuery(id+"F0.wireOp",EDGE,"E66.sketch_text.stroke-17"),sQuery(id+"F0.wireOp",EDGE,"E66.sketch_text.stroke-18"),sQuery(id+"F0.wireOp",EDGE,"E66.sketch_text.stroke-19"),sQuery(id+"F0.wireOp",EDGE,"E66.sketch_text.stroke-20"),sQuery(id+"F0.wireOp",EDGE,"E66.sketch_text.stroke-21"),sQuery(id+"F0.wireOp",EDGE,"E66.sketch_text.stroke-22"),sQuery(id+"F0.wireOp",EDGE,"E66.sketch_text.stroke-23"),sQuery(id+"F0.wireOp",EDGE,"E66.sketch_text.stroke-24"),sQuery(id+"F0.wireOp",EDGE,"E66.sketch_text.stroke-25"),sQuery(id+"F0.wireOp",EDGE,"E66.sketch_text.stroke-26"),sQuery(id+"F0.wireOp",EDGE,"E66.sketch_text.stroke-27"),sQuery(id+"F0.wireOp",EDGE,"E66.sketch_text.stroke-28"),sQuery(id+"F0.wireOp",EDGE,"E66.sketch_text.stroke-29"),sQuery(id+"F0.wireOp",EDGE,"E66.sketch_text.stroke-30"),sQuery(id+"F0.wireOp",EDGE,"E66.sketch_text.stroke-31"),sQuery(id+"F0.wireOp",EDGE,"E66.sketch_text.stroke-32"),sQuery(id+"F0.wireOp",EDGE,"E66.sketch_text.stroke-33"),sQuery(id+"F0.wireOp",EDGE,"E66.sketch_text.stroke-34"),sQuery(id+"F0.wireOp",EDGE,"E66.sketch_text.stroke-35"),sQuery(id+"F0.wireOp",EDGE,"E66.sketch_text.stroke-36"),sQuery(id+"F0.wireOp",EDGE,"E66.sketch_text.stroke-37"),sQuery(id+"F0.wireOp",EDGE,"E66.sketch_text.stroke-38"),sQuery(id+"F0.wireOp",EDGE,"E66.sketch_text.stroke-39"),sQuery(id+"F0.wireOp",EDGE,"E66.sketch_text.stroke-40"),sQuery(id+"F0.wireOp",EDGE,"E66.sketch_text.stroke-41"),sQuery(id+"F0.wireOp",EDGE,"E66.sketch_text.stroke-42"),sQuery(id+"F0.wireOp",EDGE,"E66.sketch_text.stroke-43"),sQuery(id+"F0.wireOp",EDGE,"E66.sketch_text.stroke-44"),sQuery(id+"F0.wireOp",EDGE,"E66.sketch_text.stroke-45"),sQuery(id+"F0.wireOp",EDGE,"E66.sketch_text.stroke-46"),sQuery(id+"F0.wireOp",EDGE,"E66.sketch_text.stroke-47"),sQuery(id+"F0.wireOp",EDGE,"E66.sketch_text.stroke-48"),sQuery(id+"F0.wireOp",EDGE,"E66.sketch_text.stroke-49"),sQuery(id+"F0.wireOp",EDGE,"E66.sketch_text.stroke-50"),sQuery(id+"F0.wireOp",EDGE,"E66.sketch_text.stroke-51"),sQuery(id+"F0.wireOp",EDGE,"E66.sketch_text.stroke-52"),sQuery(id+"F0.wireOp",EDGE,"E66.sketch_text.stroke-53"),sQuery(id+"F0.wireOp",EDGE,"E66.sketch_text.stroke-54"),sQuery(id+"F0.wireOp",EDGE,"E66.sketch_text.stroke-55"),sQuery(id+"F0.wireOp",EDGE,"E66.sketch_text.stroke-56"),sQuery(id+"F0.wireOp",EDGE,"E66.sketch_text.stroke-57"),sQuery(id+"F0.wireOp",EDGE,"E66.sketch_text.stroke-58"),sQuery(id+"F0.wireOp",EDGE,"E66.sketch_text.stroke-59"),sQuery(id+"F0.wireOp",EDGE,"E66.sketch_text.stroke-60"),sQuery(id+"F0.wireOp",EDGE,"E66.sketch_text.stroke-61"),sQuery(id+"F0.wireOp",EDGE,"E66.sketch_text.stroke-62"),sQuery(id+"F0.wireOp",EDGE,"E66.sketch_text.stroke-63"),sQuery(id+"F0.wireOp",EDGE,"E66.sketch_text.stroke-64"),sQuery(id+"F0.wireOp",EDGE,"E66.sketch_text.stroke-65"),sQuery(id+"F0.wireOp",EDGE,"E66.sketch_text.stroke-66"),sQuery(id+"F0.wireOp",EDGE,"E66.sketch_text.stroke-67"),sQuery(id+"F0.wireOp",EDGE,"E66.sketch_text.stroke-68")])],"isStart":false});
            var sketch = newSketch(context, id + "F17", { "sketchPlane" : qUnion([Q0])});
            skLineSegment(sketch, "E95.0", {"start": v(-6.3, 15.5) * mm, "end": v(31.7, 15.5) * mm});
            skCircle(sketch, "E96.0", {"center": v(1.7, 11.5) * mm, "radius": 2.5 * mm});
            skLineSegment(sketch, "E97.0", {"start": v(3.1, 5) * mm, "end": v(-0.9, 9) * mm});
            skArc(sketch, "E98.0", {"start": v(36.7, 10.5) * mm, "mid": v(35.23, 14.04) * mm, "end": v(31.7, 15.5) * mm});
            skLineSegment(sketch, "E99.0", {"start": v(36.7, 10.5) * mm, "end": v(36.7, -10.5) * mm});
            skArc(sketch, "E100.0", {"start": v(31.7, -15.5) * mm, "mid": v(35.23, -14.04) * mm, "end": v(36.7, -10.5) * mm});
            skLineSegment(sketch, "E101.0", {"start": v(-6.3, -15.5) * mm, "end": v(31.7, -15.5) * mm});
            skCircle(sketch, "E102.0", {"center": v(21.7, -11.5) * mm, "radius": 2.5 * mm});
            skArc(sketch, "E103", {"start": v(6.6, 12.44) * mm, "mid": v(5.93, 14.15) * mm, "end": v(4.7, 15.5) * mm});
            skLineSegment(sketch, "E104.0", {"start": v(-11.3, 9) * mm, "end": v(-0.9, 9) * mm});
            skArc(sketch, "E105.0", {"start": v(-6.3, 15.5) * mm, "mid": v(-9.84, 14.04) * mm, "end": v(-11.3, 10.5) * mm});
            skLineSegment(sketch, "E106", {"start": v(-11.3, 10.5) * mm, "end": v(-4.3, 10.5) * mm});
            skArc(sketch, "E107", {"start": v(17.92, -14.78) * mm, "mid": v(18.29, -15.16) * mm, "end": v(18.7, -15.5) * mm});
            skArc(sketch, "E108.0", {"start": v(20.7, 3.12) * mm, "mid": v(22.1, 2.34) * mm, "end": v(22.44, 3.92) * mm});
            skArc(sketch, "E109.0", {"start": v(20.7, -3.25) * mm, "mid": v(22.05, -2.32) * mm, "end": v(22.44, -3.92) * mm});
            skArc(sketch, "E110.0", {"start": v(21.7, -0.75) * mm, "mid": v(22.44, 0) * mm, "end": v(21.7, 0.75) * mm});
            skLineSegment(sketch, "E111", {"start": v(21.7, 0) * mm, "end": v(26.36, 0) * mm});
            skLineSegment(sketch, "E112", {"start": v(26.36, 0) * mm, "end": v(21.7, 3.25) * mm});
            skLineSegment(sketch, "E113", {"start": v(26.36, 0) * mm, "end": v(21.7, -3.25) * mm});
            skPoint(sketch, "E114.0", {"position": v(24.5, 1.09) * mm});
            skPoint(sketch, "E115.0", {"position": v(31.7, 0) * mm});
            skPoint(sketch, "E116.0", {"position": v(23.76, 0.85) * mm});
            skArc(sketch, "E117.0.startCap", {"start": v(26.65, 0.41) * mm, "mid": v(26.77, -0.29) * mm, "end": v(26.07, -0.41) * mm});
            skArc(sketch, "E117.0.endCap", {"start": v(21.4, 2.84) * mm, "mid": v(21.28, 3.54) * mm, "end": v(21.98, 3.66) * mm});
            skLineSegment(sketch, "E117.0.left", {"start": v(26.07, -0.41) * mm, "end": v(21.4, 2.84) * mm});
            skLineSegment(sketch, "E117.0.right", {"start": v(26.65, 0.41) * mm, "end": v(21.98, 3.66) * mm});
            skArc(sketch, "E117.1.startCap", {"start": v(26.07, 0.41) * mm, "mid": v(26.77, 0.29) * mm, "end": v(26.65, -0.41) * mm});
            skArc(sketch, "E117.1.endCap", {"start": v(21.98, -3.66) * mm, "mid": v(21.28, -3.54) * mm, "end": v(21.4, -2.84) * mm});
            skLineSegment(sketch, "E117.1.left", {"start": v(26.65, -0.41) * mm, "end": v(21.98, -3.66) * mm});
            skLineSegment(sketch, "E117.1.right", {"start": v(26.07, 0.41) * mm, "end": v(21.4, -2.84) * mm});
            skArc(sketch, "E117.2.startCap", {"start": v(21.7, -0.5) * mm, "mid": v(21.2, 0) * mm, "end": v(21.7, 0.5) * mm});
            skArc(sketch, "E117.2.endCap", {"start": v(26.36, 0.5) * mm, "mid": v(26.86, 0) * mm, "end": v(26.36, -0.5) * mm});
            skLineSegment(sketch, "E117.2.left", {"start": v(21.7, 0.5) * mm, "end": v(26.36, 0.5) * mm});
            skLineSegment(sketch, "E117.2.right", {"start": v(21.7, -0.5) * mm, "end": v(26.36, -0.5) * mm});
            skPoint(sketch, "E118", {"position": v(24.5, 1.3) * mm});
            skPoint(sketch, "E119", {"position": v(23.76, -2.42) * mm});
            skPoint(sketch, "E120", {"position": v(24.5, -1.3) * mm});
            skArc(sketch, "E121.0", {"start": v(28.7, 5) * mm, "mid": v(23.7, 0) * mm, "end": v(28.7, -5) * mm});
            skLineSegment(sketch, "E122.0", {"start": v(31.7, 5) * mm, "end": v(28.7, 5) * mm});
            skLineSegment(sketch, "E123.0.0", {"start": v(28.7, -5) * mm, "end": v(31.7, -5) * mm});
            skLineSegment(sketch, "E123.0.1", {"start": v(31.7, -5) * mm, "end": v(31.7, 5) * mm});
            skLineSegment(sketch, "E124", {"start": v(8.55, 10.82) * mm, "end": v(16.52, 10.75) * mm});
            skLineSegment(sketch, "E125", {"start": v(36.7, 9.58) * mm, "end": v(36.7, 5.47) * mm});
            skLineSegment(sketch, "E126", {"start": v(35.7, 4.47) * mm, "end": v(34.3, 4.47) * mm});
            skLineSegment(sketch, "E127", {"start": v(33.3, 3.47) * mm, "end": v(33.3, -5.6) * mm});
            skLineSegment(sketch, "E128", {"start": v(32.3, -6.6) * mm, "end": v(26.25, -6.6) * mm});
            skLineSegment(sketch, "E129", {"start": v(0.74, -13.4) * mm, "end": v(0.74, -11.6) * mm});
            skLineSegment(sketch, "E130", {"start": v(1.74, -10.6) * mm, "end": v(5.44, -10.6) * mm});
            skLineSegment(sketch, "E131", {"start": v(6.44, -11.6) * mm, "end": v(6.44, -13.44) * mm});
            skLineSegment(sketch, "E132", {"start": v(7.44, -14.44) * mm, "end": v(17.17, -14.44) * mm});
            skLineSegment(sketch, "E133", {"start": v(-0.26, -14.4) * mm, "end": v(-9.43, -14.4) * mm});
            skLineSegment(sketch, "E134", {"start": v(17.5, 9.75) * mm, "end": v(17.5, 7.6) * mm});
            skLineSegment(sketch, "E135", {"start": v(18.5, 6.6) * mm, "end": v(20.02, 6.6) * mm});
            skLineSegment(sketch, "E136", {"start": v(21.02, 7.6) * mm, "end": v(21.02, 9.7) * mm});
            skLineSegment(sketch, "E137.trimOffspring", {"start": v(22.03, 10.7) * mm, "end": v(35.7, 10.58) * mm});
            skArc(sketch, "E138.trimOffspring", {"start": v(-1.3, 15.5) * mm, "mid": v(-2.78, 13.74) * mm, "end": v(-3.3, 11.5) * mm});
            skArc(sketch, "E139.trimOffspring", {"start": v(-2.64, 9) * mm, "mid": v(-0.84, 7.2) * mm, "end": v(1.6, 6.5) * mm});
            skArc(sketch, "E140.trimOffspring", {"start": v(24.7, -15.5) * mm, "mid": v(26.66, -12.05) * mm, "end": v(25.5, -8.25) * mm});
            skPoint(sketch, "E141.orphan", {"position": v(6.44, -15.5) * mm});
            skPoint(sketch, "E142.orphan", {"position": v(0.74, -15.5) * mm});
            skPoint(sketch, "E143.visualSharp", {"position": v(-3.2, 10.5) * mm});
            skArc(sketch, "E143.filletArc", {"start": v(-4.3, 10.5) * mm, "mid": v(-3.6, 10.8) * mm, "end": v(-3.3, 11.5) * mm});
            skPoint(sketch, "E144.visualSharp", {"position": v(6.65, 10.84) * mm});
            skArc(sketch, "E144.filletArc", {"start": v(6.6, 12.44) * mm, "mid": v(7.29, 11.28) * mm, "end": v(8.55, 10.82) * mm});
            skPoint(sketch, "E145.visualSharp", {"position": v(17.5, 10.74) * mm});
            skArc(sketch, "E145.filletArc", {"start": v(17.5, 9.75) * mm, "mid": v(17.22, 10.45) * mm, "end": v(16.52, 10.75) * mm});
            skPoint(sketch, "E146.visualSharp", {"position": v(21.02, 6.6) * mm});
            skArc(sketch, "E146.filletArc", {"start": v(20.02, 6.6) * mm, "mid": v(20.73, 6.9) * mm, "end": v(21.02, 7.6) * mm});
            skPoint(sketch, "E147.visualSharp", {"position": v(21.02, 10.7) * mm});
            skArc(sketch, "E147.filletArc", {"start": v(22.03, 10.7) * mm, "mid": v(21.32, 10.4) * mm, "end": v(21.02, 9.7) * mm});
            skPoint(sketch, "E148.visualSharp", {"position": v(36.7, 10.57) * mm});
            skArc(sketch, "E148.filletArc", {"start": v(36.7, 9.58) * mm, "mid": v(36.4, 10.28) * mm, "end": v(35.7, 10.58) * mm});
            skPoint(sketch, "E149.visualSharp", {"position": v(33.3, 4.47) * mm});
            skArc(sketch, "E149.filletArc", {"start": v(34.3, 4.47) * mm, "mid": v(33.59, 4.18) * mm, "end": v(33.3, 3.47) * mm});
            skPoint(sketch, "E150.visualSharp", {"position": v(33.3, -6.6) * mm});
            skArc(sketch, "E150.filletArc", {"start": v(32.3, -6.6) * mm, "mid": v(33, -6.3) * mm, "end": v(33.3, -5.6) * mm});
            skPoint(sketch, "E151.visualSharp", {"position": v(17.65, -14.44) * mm});
            skArc(sketch, "E151.filletArc", {"start": v(17.92, -14.78) * mm, "mid": v(17.58, -14.53) * mm, "end": v(17.17, -14.44) * mm});
            skPoint(sketch, "E152.visualSharp", {"position": v(6.44, -10.6) * mm});
            skArc(sketch, "E152.filletArc", {"start": v(6.44, -11.6) * mm, "mid": v(6.15, -10.9) * mm, "end": v(5.44, -10.6) * mm});
            skPoint(sketch, "E153.visualSharp", {"position": v(0.74, -14.4) * mm});
            skArc(sketch, "E153.filletArc", {"start": v(-0.26, -14.4) * mm, "mid": v(0.45, -14.1) * mm, "end": v(0.74, -13.4) * mm});
            skPoint(sketch, "E154.visualSharp", {"position": v(22.69, -6.6) * mm});
            skArc(sketch, "E154.filletArc", {"start": v(26.25, -6.6) * mm, "mid": v(25.35, -7.18) * mm, "end": v(25.5, -8.25) * mm});
            skPoint(sketch, "E155.visualSharp", {"position": v(36.7, 4.47) * mm});
            skArc(sketch, "E155.filletArc", {"start": v(35.7, 4.47) * mm, "mid": v(36.4, 4.77) * mm, "end": v(36.7, 5.47) * mm});
            skPoint(sketch, "E156.visualSharp", {"position": v(17.5, 6.6) * mm});
            skArc(sketch, "E156.filletArc", {"start": v(17.5, 7.6) * mm, "mid": v(17.8, 6.9) * mm, "end": v(18.5, 6.6) * mm});
            skPoint(sketch, "E157.visualSharp", {"position": v(0.74, -10.6) * mm});
            skArc(sketch, "E157.filletArc", {"start": v(1.74, -10.6) * mm, "mid": v(1.03, -10.9) * mm, "end": v(0.74, -11.6) * mm});
            skPoint(sketch, "E158.visualSharp", {"position": v(6.44, -14.44) * mm});
            skArc(sketch, "E158.filletArc", {"start": v(6.44, -13.44) * mm, "mid": v(6.74, -14.15) * mm, "end": v(7.44, -14.44) * mm});
            skSolve(sketch);
        }
        {
            var Q0;
            {var subQ1=sQuery(id+"F17.wireOp",EDGE,"E105.0");Q0=makeQuery(id+"F17.imprint","IMPRINT",FACE,{"disambiguationData":[TD([[makeQuery(id+"F17.imprint","IMPRINT",EDGE,{"derivedFrom":subQ1}),1.0]])]});}
            var Q1;
            {var subQ0=sQuery(id+"F17.wireOp",EDGE,"E98.0");Q1=makeQuery(id+"F17.imprint","IMPRINT",FACE,{"disambiguationData":[TD([[makeQuery(id+"F17.imprint","IMPRINT",EDGE,{"derivedFrom":subQ0}),1.0]])]});}
            var Q2;
            {var subQ0=sQuery(id+"F17.wireOp",EDGE,"E100.0");Q2=makeQuery(id+"F17.imprint","IMPRINT",FACE,{"disambiguationData":[TD([[makeQuery(id+"F17.imprint","IMPRINT",EDGE,{"derivedFrom":subQ0}),1.0]])]});}
            var Q3;
            {var subQ1=sQuery(id+"F17.wireOp",EDGE,"E107");Q3=makeQuery(id+"F17.imprint","IMPRINT",FACE,{"disambiguationData":[TD([[makeQuery(id+"F17.imprint","IMPRINT",EDGE,{"derivedFrom":subQ1}),-1.0]])]});}
            extrude(context, id + "F18", {"entities" : qUnion([Q0, Q1, Q2, Q3]), "operationType" : NewBodyOperationType.REMOVE, "oppositeDirection" : true, "depth" : 2.7 * mm});
        }
        {
            var Q0;
            {var subQ0=sQuery(id+"F17.wireOp",EDGE,"E112");var subQ1=sQuery(id+"F17.wireOp",EDGE,"E108.0");var subQ2=makeQuery(id+"F17.imprint","INTERSECT",VERTEX,{"derivedFrom":[subQ1,subQ0]});Q0=makeQuery(id+"F17.imprint","IMPRINT",FACE,{"disambiguationData":[TD([[makeQuery(id+"F17.imprint","IMPRINT",EDGE,{"disambiguationData":[TD([[subQ2,-1.0]])],"derivedFrom":subQ1}),-1.0]])]});}
            var Q1;
            {var subQ0=sQuery(id+"F17.wireOp",EDGE,"E117.0.left");var subQ1=sQuery(id+"F17.wireOp",EDGE,"E108.0");var subQ2=makeQuery(id+"F17.imprint","INTERSECT",VERTEX,{"derivedFrom":[subQ1,subQ0]});Q1=makeQuery(id+"F17.imprint","IMPRINT",FACE,{"disambiguationData":[TD([[makeQuery(id+"F17.imprint","IMPRINT",EDGE,{"disambiguationData":[TD([[subQ2,-1.0]])],"derivedFrom":subQ1}),-1.0]])]});}
            var Q2;
            {var subQ0=sQuery(id+"F17.wireOp",EDGE,"E111");var subQ1=sQuery(id+"F17.wireOp",EDGE,"E110.0");var subQ2=makeQuery(id+"F17.imprint","INTERSECT",VERTEX,{"derivedFrom":[subQ1,subQ0]});Q2=makeQuery(id+"F17.imprint","IMPRINT",FACE,{"disambiguationData":[TD([[makeQuery(id+"F17.imprint","IMPRINT",EDGE,{"disambiguationData":[TD([[subQ2,-1.0]])],"derivedFrom":subQ1}),-1.0]])]});}
            var Q3;
            {var subQ0=sQuery(id+"F17.wireOp",EDGE,"E111");var subQ1=sQuery(id+"F17.wireOp",EDGE,"E110.0");var subQ2=makeQuery(id+"F17.imprint","INTERSECT",VERTEX,{"derivedFrom":[subQ1,subQ0]});Q3=makeQuery(id+"F17.imprint","IMPRINT",FACE,{"disambiguationData":[TD([[makeQuery(id+"F17.imprint","IMPRINT",EDGE,{"disambiguationData":[TD([[subQ2,1.0]])],"derivedFrom":subQ1}),-1.0]])]});}
            var Q4;
            {var subQ0=sQuery(id+"F17.wireOp",EDGE,"E117.1.right");var subQ1=sQuery(id+"F17.wireOp",EDGE,"E109.0");var subQ2=makeQuery(id+"F17.imprint","INTERSECT",VERTEX,{"derivedFrom":[subQ1,subQ0]});Q4=makeQuery(id+"F17.imprint","IMPRINT",FACE,{"disambiguationData":[TD([[makeQuery(id+"F17.imprint","IMPRINT",EDGE,{"disambiguationData":[TD([[subQ2,-1.0]])],"derivedFrom":subQ1}),1.0]])]});}
            var Q5;
            {var subQ0=sQuery(id+"F17.wireOp",EDGE,"E113");var subQ1=sQuery(id+"F17.wireOp",EDGE,"E109.0");var subQ2=makeQuery(id+"F17.imprint","INTERSECT",VERTEX,{"derivedFrom":[subQ1,subQ0]});Q5=makeQuery(id+"F17.imprint","IMPRINT",FACE,{"disambiguationData":[TD([[makeQuery(id+"F17.imprint","IMPRINT",EDGE,{"disambiguationData":[TD([[subQ2,-1.0]])],"derivedFrom":subQ1}),1.0]])]});}
            var Q6;
            {var subQ1=sQuery(id+"F17.wireOp",EDGE,"E117.1.endCap");Q6=makeQuery(id+"F17.imprint","IMPRINT",FACE,{"disambiguationData":[TD([[makeQuery(id+"F17.imprint","IMPRINT",EDGE,{"derivedFrom":subQ1}),-1.0]])]});}
            var Q7;
            {var subQ1=sQuery(id+"F17.wireOp",EDGE,"E117.2.startCap");Q7=makeQuery(id+"F17.imprint","IMPRINT",FACE,{"disambiguationData":[TD([[makeQuery(id+"F17.imprint","IMPRINT",EDGE,{"derivedFrom":subQ1}),-1.0]])]});}
            var Q8;
            {var subQ1=sQuery(id+"F17.wireOp",EDGE,"E117.0.endCap");Q8=makeQuery(id+"F17.imprint","IMPRINT",FACE,{"disambiguationData":[TD([[makeQuery(id+"F17.imprint","IMPRINT",EDGE,{"derivedFrom":subQ1}),-1.0]])]});}
            extrude(context, id + "F19", {"entities" : qUnion([Q0, Q1, Q2, Q3, Q4, Q5, Q6, Q7, Q8]), "operationType" : NewBodyOperationType.REMOVE, "oppositeDirection" : true, "depth" : 1.5 * mm});
        }
        {
            var Q0;
            Q0=makeQuery(id+"F1.opExtrude","SWEPT_EDGE",EDGE,{"disambiguationData":[OSD([sQuery(id+"F0.wireOp",EDGE,"E56.bottom"),sQuery(id+"F0.wireOp",EDGE,"E57")])]});
            var Q1;
            Q1=makeQuery(id+"F1.opExtrude","SWEPT_EDGE",EDGE,{"disambiguationData":[OSD([sQuery(id+"F0.wireOp",EDGE,"E56.top"),sQuery(id+"F0.wireOp",EDGE,"E58")])]});
            var Q2;
            Q2=makeQuery(id+"F1.opExtrude","SWEPT_EDGE",EDGE,{"disambiguationData":[OSD([sQuery(id+"F0.wireOp",EDGE,"E32.bottom"),sQuery(id+"F0.wireOp",EDGE,"E57")])]});
            var Q3;
            Q3=makeQuery(id+"F1.opExtrude","SWEPT_EDGE",EDGE,{"disambiguationData":[OSD([sQuery(id+"F0.wireOp",EDGE,"E32.top"),sQuery(id+"F0.wireOp",EDGE,"E58")])]});
            var Q4;
            Q4=makeQuery(id+"F1.opExtrude","SWEPT_EDGE",EDGE,{"disambiguationData":[OSD([sQuery(id+"F0.wireOp",EDGE,"E25"),sQuery(id+"F0.wireOp",EDGE,"E28")])]});
            var Q5;
            Q5=makeQuery(id+"F1.opExtrude","SWEPT_EDGE",EDGE,{"disambiguationData":[OSD([sQuery(id+"F0.wireOp",EDGE,"E26"),sQuery(id+"F0.wireOp",EDGE,"E27")])]});
            var Q6;
            Q6=makeQuery(id+"F1.opExtrude","SWEPT_EDGE",EDGE,{"disambiguationData":[OSD([sQuery(id+"F0.wireOp",EDGE,"E33.bottom"),sQuery(id+"F0.wireOp",EDGE,"E45")])]});
            var Q7;
            Q7=makeQuery(id+"F1.opExtrude","SWEPT_EDGE",EDGE,{"disambiguationData":[OSD([sQuery(id+"F0.wireOp",EDGE,"E46"),sQuery(id+"F0.wireOp",EDGE,"E47")])]});
            fillet(context, id + "F20", {"entities" : qUnion([Q0, Q1, Q2, Q3, Q4, Q5, Q6, Q7]), "radius" : 3 * mm, "tangentPropagation" : true, "allowEdgeOverflow" : false});
        }
    });
